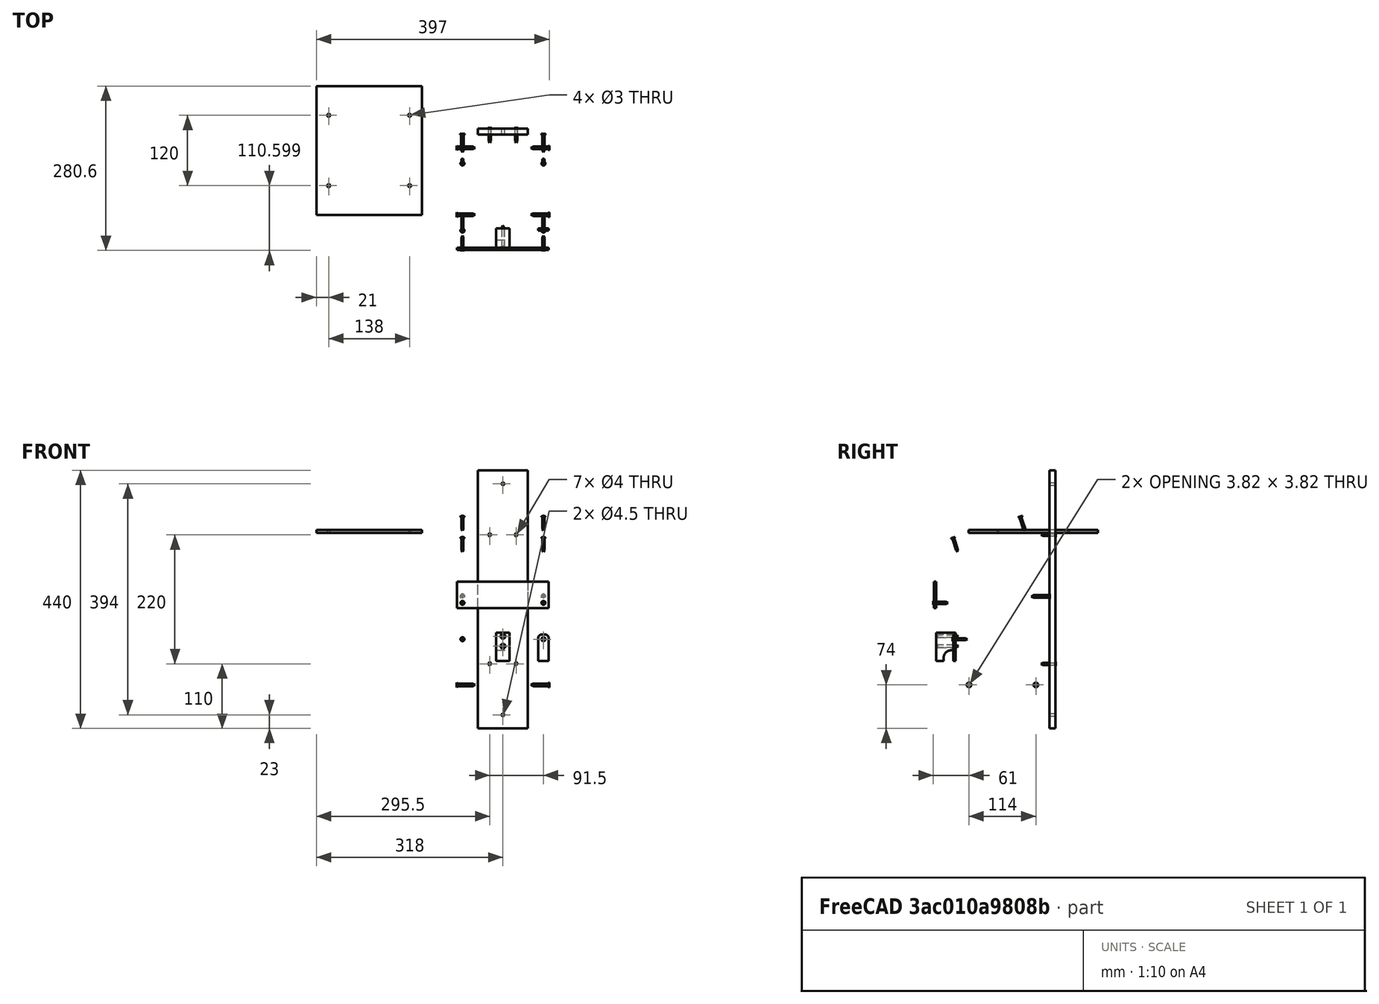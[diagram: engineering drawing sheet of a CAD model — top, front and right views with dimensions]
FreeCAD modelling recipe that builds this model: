
FCSTD DOCUMENT  (FreeCAD 1.0R39109 (Git))
Label: Nistkasten_LC_32__Final
License: All rights reserved
LicenseURL: http://en.wikipedia.org/wiki/All_rights_reserved
objects: TechDraw::DrawViewDimension×37, Sketcher::SketchObject×25, PartDesign::Body×25, Part::FeaturePython×20, TechDraw::DrawViewAnnotation×17, PartDesign::Pad×14, TechDraw::DrawProjGroupItem×13, PartDesign::FeatureBase×10, Part::Part2DObjectPython×10, PartDesign::Pocket×10, App::DocumentObjectGroup×6, PartDesign::Chamfer×6, TechDraw::DrawSVGTemplate×5, TechDraw::DrawProjGroup×5, TechDraw::DrawPage×5, Spreadsheet::Sheet×1, PartDesign::Fillet×1, TechDraw::DrawViewSection×1
note: 268 computed .brp shape members not serialized (recipe doc carries the construction recipe); baked Part::Feature solids carry a one-line shape summary decoded from their .brp

FEATURE [Sketcher::SketchObject] Sketch001
  ArcFitTolerance = 0
  AttachmentSupport = -> [XY_Plane001]
  FullyConstrained = true
  MakeInternals = false
  MapMode = 5
  expr: Constraints[42] = 120 mm / 2
  expr: Constraints[43] = 120 mm / 2
  expr: Constraints[8] = 120 mm + 2 * <<Parameter>>.Brettdicke
  expr: Constraints[9] = 124 mm + 2 * <<Parameter>>.Brettdicke
  sketch-geometry (16):
    g0: LineSegment [constr] StartX=-78 StartY=80 StartZ=0 EndX=78 EndY=80 EndZ=0
    g1: LineSegment [constr] StartX=78 StartY=80 StartZ=0 EndX=78 EndY=-80 EndZ=0
    g2: LineSegment [constr] StartX=78 StartY=-80 StartZ=0 EndX=-78 EndY=-80 EndZ=0
    g3: LineSegment [constr] StartX=-78 StartY=-80 StartZ=0 EndX=-78 EndY=80 EndZ=0
    g4: LineSegment StartX=-78 StartY=-25 StartZ=0 EndX=-78 EndY=25 EndZ=0
    g5: LineSegment StartX=-78 StartY=25 StartZ=0 EndX=-60 EndY=25 EndZ=0
    g6: LineSegment StartX=-60 StartY=25 StartZ=0 EndX=-60 EndY=80 EndZ=0
    g7: LineSegment StartX=-60 StartY=80 StartZ=0 EndX=60 EndY=80 EndZ=0
    g8: LineSegment StartX=60 StartY=80 StartZ=0 EndX=60 EndY=25 EndZ=0
    g9: LineSegment StartX=60 StartY=25 StartZ=0 EndX=78 EndY=25 EndZ=0
    g10: LineSegment StartX=78 StartY=25 StartZ=0 EndX=78 EndY=-25 EndZ=0
    g11: LineSegment StartX=78 StartY=-25 StartZ=0 EndX=60 EndY=-25 EndZ=0
    g12: LineSegment StartX=60 StartY=-25 StartZ=0 EndX=60 EndY=-80 EndZ=0
    g13: LineSegment StartX=60 StartY=-80 StartZ=0 EndX=-60 EndY=-80 EndZ=0
    g14: LineSegment StartX=-60 StartY=-80 StartZ=0 EndX=-60 EndY=-25 EndZ=0
    g15: LineSegment StartX=-60 StartY=-25 StartZ=0 EndX=-78 EndY=-25 EndZ=0
  constraints (46):
    c: Coincident(g0,g1)
    c: Coincident(g1,g2)
    c: Coincident(g2,g3)
    c: Coincident(g3,g0)
    c: Horizontal(g2)
    c: Vertical(g1)
    c: Symmetric(g0,g0,g-2)
    c: Symmetric(g2,g0,g-1)
    c: DistanceX(g2,g2) = 156
    c: DistanceY(g3,g3) = 160
    c: PointOnObject(g4,g3)
    c: PointOnObject(g4,g3)
    c: Coincident(g4,g5)
    c: Horizontal(g5)
    c: Coincident(g5,g6)
    c: PointOnObject(g6,g0)
    c: Vertical(g6)
    c: Coincident(g6,g7)
    c: PointOnObject(g7,g0)
    c: Coincident(g7,g8)
    c: Vertical(g8)
    c: Coincident(g8,g9)
    c: PointOnObject(g9,g1)
    c: Horizontal(g9)
    c: Coincident(g9,g10)
    c: PointOnObject(g10,g1)
    c: Coincident(g10,g11)
    c: Horizontal(g11)
    c: Coincident(g11,g12)
    c: PointOnObject(g12,g2)
    c: Vertical(g12)
    c: Coincident(g12,g13)
    c: PointOnObject(g13,g2)
    c: Coincident(g13,g14)
    c: Vertical(g14)
    c: Coincident(g14,g15)
    c: Coincident(g15,g4)
    c: Horizontal(g15)
    c: DistanceY(g4,g4) = 50
    c: Equal(g4,g10)
    c: DistanceY(g6,g6) = 55
    c: Equal(g8,g6)
    c: DistanceX(g14,g-1) = 60
    c: DistanceX(g-1,g11) = 60
    c: Equal(g15,g5)
    c: Equal(g5,g9)
FEATURE [Spreadsheet::Sheet] Spreadsheet  label="Parameter"
  cells = A2='Parameter; A3='Brettdicke; B3(Brettdicke)==18 mm
FEATURE [PartDesign::Pad] Pad001
  Direction = (0,0,1)
  Length = 18
  Length2 = 10
  Profile = -> Sketch001
  ReferenceAxis = -> Sketch001 [N_Axis]
  Reversed = true
  Suppressed = false
  Type = 0
  expr: Length = <<Parameter>>.Brettdicke
FEATURE [Sketcher::SketchObject] Sketch002
  ArcFitTolerance = 0
  AttachmentSupport = -> [XZ_Plane002]
  FullyConstrained = true
  MakeInternals = false
  MapMode = 5
  Placement = pos=(0,0,0) rot=(1,0,0;1.5708rad)
  expr: Constraints[39] = 156 mm - 2 * <<Parameter>>.Brettdicke
  expr: Constraints[9] = 120 mm + 2 * <<Parameter>>.Brettdicke
  sketch-geometry (16):
    g0: LineSegment [constr] StartX=-78 StartY=0 StartZ=0 EndX=78 EndY=0 EndZ=0
    g1: LineSegment [constr] StartX=78 StartY=0 StartZ=0 EndX=78 EndY=282 EndZ=0
    g2: LineSegment [constr] StartX=78 StartY=282 StartZ=0 EndX=-78 EndY=282 EndZ=0
    g3: LineSegment [constr] StartX=-78 StartY=282 StartZ=0 EndX=-78 EndY=0 EndZ=0
    g4: LineSegment StartX=-60 StartY=0 StartZ=0 EndX=-60 EndY=102 EndZ=0
    g5: LineSegment StartX=-60 StartY=102 StartZ=0 EndX=-78 EndY=102 EndZ=0
    g6: LineSegment StartX=-78 StartY=102 StartZ=0 EndX=-78 EndY=182 EndZ=0
    g7: LineSegment StartX=-78 StartY=182 StartZ=0 EndX=-60 EndY=182 EndZ=0
    g8: LineSegment StartX=-60 StartY=182 StartZ=0 EndX=-60 EndY=282 EndZ=0
    g9: LineSegment StartX=-60 StartY=282 StartZ=0 EndX=60 EndY=282 EndZ=0
    g10: LineSegment StartX=60 StartY=282 StartZ=0 EndX=60 EndY=182 EndZ=0
    g11: LineSegment StartX=60 StartY=182 StartZ=0 EndX=78 EndY=182 EndZ=0
    g12: LineSegment StartX=78 StartY=182 StartZ=0 EndX=78 EndY=102 EndZ=0
    g13: LineSegment StartX=78 StartY=102 StartZ=0 EndX=60 EndY=102 EndZ=0
    g14: LineSegment StartX=60 StartY=102 StartZ=0 EndX=60 EndY=0 EndZ=0
    g15: LineSegment StartX=60 StartY=0 StartZ=0 EndX=-60 EndY=0 EndZ=0
  constraints (45):
    c: Coincident(g0,g1)
    c: Coincident(g1,g2)
    c: Coincident(g2,g3)
    c: Coincident(g3,g0)
    c: Horizontal(g2)
    c: Vertical(g1)
    c: Vertical(g3)
    c: PointOnObject(g0,g-1)
    c: Symmetric(g0,g0,g-2)
    c: DistanceX(g0,g0) = 156
    c: DistanceY(g3,g3) = 282
    c: PointOnObject(g4,g0)
    c: Vertical(g4)
    c: Coincident(g4,g5)
    c: PointOnObject(g5,g3)
    c: Horizontal(g5)
    c: Coincident(g5,g6)
    c: PointOnObject(g6,g3)
    c: Coincident(g6,g7)
    c: Horizontal(g7)
    c: Coincident(g7,g8)
    c: PointOnObject(g8,g2)
    c: Vertical(g8)
    c: Coincident(g8,g9)
    c: Coincident(g9,g10)
    c: Vertical(g10)
    c: Coincident(g10,g11)
    c: PointOnObject(g11,g1)
    c: Horizontal(g11)
    c: Coincident(g11,g12)
    c: PointOnObject(g12,g1)
    c: Coincident(g12,g13)
    c: Horizontal(g13)
    c: Coincident(g13,g14)
    c: Vertical(g14)
    c: Coincident(g14,g15)
    c: Coincident(g15,g4)
    c: Symmetric(g4,g14,g-2)
    c: Symmetric(g8,g9,g-2)
    c: DistanceX(g15,g15) = 120
    c: DistanceY(g6,g6) = 80
    c: Equal(g6,g12)
    c: DistanceY(g4,g4) = 102
    c: Equal(g4,g14)
    c: Equal(g5,g7)
FEATURE [PartDesign::Pad] Pad002
  Direction = (0,-1,2e-16)
  Length = 18
  Length2 = 10
  Placement = pos=(0,0,0) rot=(1,0,0;1.5708rad)
  Profile = -> Sketch002
  ReferenceAxis = -> Sketch002 [N_Axis]
  Reversed = true
  Suppressed = false
  Type = 0
  expr: Length = <<Parameter>>.Brettdicke
FEATURE [Sketcher::SketchObject] Sketch003
  ArcFitTolerance = 0
  AttachmentSupport = -> [YZ_Plane003]
  FullyConstrained = true
  MakeInternals = false
  MapMode = 5
  Placement = pos=(0,0,0) rot=(0.57735,0.57735,0.57735;2.0944rad)
  expr: Constraints[33] = <<Parameter>>.Brettdicke
  expr: Constraints[35] = <<Parameter>>.Brettdicke
  expr: Constraints[36] = <<Parameter>>.Brettdicke
  expr: Constraints[42] = <<Parameter>>.Brettdicke
  expr: Constraints[45] = <<Parameter>>.Brettdicke
  expr: Constraints[59] = <<Parameter>>.Brettdicke
  expr: Constraints[60] = <<Parameter>>.Brettdicke
  sketch-geometry (25):
    g0: LineSegment StartX=-80 StartY=-18 StartZ=0 EndX=-80 EndY=0 EndZ=0
    g1: LineSegment StartX=-80 StartY=0 StartZ=0 EndX=-62 EndY=0 EndZ=0
    g2: LineSegment StartX=-95 StartY=193 StartZ=0 EndX=-113 EndY=193 EndZ=0
    g3: LineSegment StartX=-113 StartY=193 StartZ=0 EndX=-113 EndY=227.2 EndZ=0
    g4: LineSegment StartX=-113 StartY=227.2 StartZ=0 EndX=62 EndY=282 EndZ=0
    g5: LineSegment StartX=62 StartY=282 StartZ=0 EndX=80 EndY=282 EndZ=0
    g6: LineSegment StartX=80 StartY=282 StartZ=0 EndX=80 EndY=182 EndZ=0
    g7: LineSegment StartX=80 StartY=182 StartZ=0 EndX=62 EndY=182 EndZ=0
    g8: LineSegment StartX=62 StartY=182 StartZ=0 EndX=62 EndY=102 EndZ=0
    g9: LineSegment StartX=62 StartY=102 StartZ=0 EndX=80 EndY=102 EndZ=0
    g10: LineSegment StartX=80 StartY=102 StartZ=0 EndX=80 EndY=-18 EndZ=0
    g11: LineSegment StartX=80 StartY=-18 StartZ=0 EndX=25 EndY=-18 EndZ=0
    g12: LineSegment StartX=25 StartY=-18 StartZ=0 EndX=25 EndY=0 EndZ=0
    g13: LineSegment StartX=25 StartY=0 StartZ=0 EndX=-25 EndY=0 EndZ=0
    g14: LineSegment StartX=-25 StartY=0 StartZ=0 EndX=-25 EndY=-18 EndZ=0
    g15: LineSegment StartX=-25 StartY=-18 StartZ=0 EndX=-80 EndY=-18 EndZ=0
    g16: LineSegment StartX=-72 StartY=140 StartZ=0 EndX=-72 EndY=158 EndZ=0
    g17: LineSegment StartX=-72 StartY=158 StartZ=0 EndX=-95 EndY=158 EndZ=0
    g18: LineSegment StartX=-95 StartY=158 StartZ=0 EndX=-95 EndY=193 EndZ=0
    g19: LineSegment StartX=-80 StartY=80 StartZ=0 EndX=-113 EndY=122 EndZ=0
    g20: LineSegment StartX=-113 StartY=122 StartZ=0 EndX=-113 EndY=140 EndZ=0
    g21: LineSegment StartX=-113 StartY=140 StartZ=0 EndX=-72 EndY=140 EndZ=0
    g22: LineSegment StartX=-62 StartY=0 StartZ=0 EndX=-62 EndY=60 EndZ=0
    g23: LineSegment StartX=-62 StartY=60 StartZ=0 EndX=-80 EndY=60 EndZ=0
    g24: LineSegment StartX=-80 StartY=60 StartZ=0 EndX=-80 EndY=80 EndZ=0
  constraints (74):
    c: PointOnObject(g0,g-1)
    c: Vertical(g0)
    c: Coincident(g0,g1)
    c: PointOnObject(g1,g-1)
    c: Horizontal(g2)
    c: Coincident(g2,g3)
    c: Vertical(g3)
    c: Coincident(g3,g4)
    c: Coincident(g4,g5)
    c: Horizontal(g5)
    c: Coincident(g5,g6)
    c: Vertical(g6)
    c: Coincident(g6,g7)
    c: Horizontal(g7)
    c: Coincident(g7,g8)
    c: Vertical(g8)
    c: Coincident(g8,g9)
    c: Horizontal(g9)
    c: Coincident(g9,g10)
    c: Vertical(g10)
    c: Coincident(g10,g11)
    c: Horizontal(g11)
    c: Coincident(g11,g12)
    c: PointOnObject(g12,g-1)
    c: Vertical(g12)
    c: Coincident(g12,g13)
    c: Coincident(g13,g14)
    c: Vertical(g14)
    c: Coincident(g14,g15)
    c: Coincident(g15,g0)
    c: Horizontal(g15)
    c: Symmetric(g13,g12,g-2)
    c: DistanceX(g13,g13) = 50
    c: DistanceY(g14,g14) = 18
    c: DistanceX(g15,g15) = 55
    c: DistanceX(g1,g1) = 18
    c: DistanceX(g2,g2) = 18
    c: Equal(g12,g14)
    c: DistanceX(g11,g11) = 55
    c: DistanceY(g8,g8) = 80
    c: DistanceY(g10,g10) = 120
    c: DistanceY(g6,g6) = 100
    c: DistanceX(g5,g5) = 18
    c: DistanceY(g3,g3) = 34.2
    c: Equal(g9,g7)
    c: DistanceX(g7,g7) = 18
    c: Vertical(g16)
    c: Coincident(g16,g17)
    c: Horizontal(g17)
    c: Coincident(g17,g18)
    c: Coincident(g18,g2)
    c: Vertical(g18)
    c: DistanceX(g17,g17) = 23
    c: DistanceY(g18,g18) = 35
    c: Coincident(g19,g20)
    c: Vertical(g20)
    c: Coincident(g20,g21)
    c: Coincident(g21,g16)
    c: Horizontal(g21)
    c: DistanceY(g20,g20) = 18
    c: DistanceY(g16,g16) = 18
    c: DistanceY(g19,g20) = 60
    c: DistanceX(g19,g19) = 33
    c: DistanceX(g21,g21) = 41
    c: Coincident(g1,g22)
    c: Vertical(g22)
    c: Coincident(g22,g23)
    c: Horizontal(g23)
    c: Coincident(g23,g24)
    c: Coincident(g24,g19)
    c: Vertical(g24)
    c: DistanceY(g0,g19) = 80
    c: DistanceY(g24,g24) = 20
    c: DistanceX(g23,g23) = 18
FEATURE [PartDesign::Pad] Pad003
  Direction = (1,0,0)
  Length = 18
  Length2 = 10
  Placement = pos=(0,0,0) rot=(0.57735,0.57735,0.57735;2.0944rad)
  Profile = -> Sketch003
  ReferenceAxis = -> Sketch003 [N_Axis]
  Reversed = true
  Suppressed = false
  Type = 0
  expr: Length = <<Parameter>>.Brettdicke
FEATURE [Sketcher::SketchObject] Sketch004
  ArcFitTolerance = 0
  AttachmentSupport = -> [XY_Plane005]
  FullyConstrained = true
  MakeInternals = false
  MapMode = 5
  expr: Constraints[20] = <<Parameter>>.Brettdicke
  sketch-geometry (8):
    g0: LineSegment StartX=-60 StartY=0 StartZ=0 EndX=60 EndY=0 EndZ=0
    g1: LineSegment StartX=78 StartY=-53 StartZ=0 EndX=-78 EndY=-53 EndZ=0
    g2: LineSegment StartX=-78 StartY=-53 StartZ=0 EndX=-78 EndY=-12 EndZ=0
    g3: LineSegment StartX=-78 StartY=-12 StartZ=0 EndX=-60 EndY=-12 EndZ=0
    g4: LineSegment StartX=-60 StartY=-12 StartZ=0 EndX=-60 EndY=0 EndZ=0
    g5: LineSegment StartX=78 StartY=-53 StartZ=0 EndX=78 EndY=-12 EndZ=0
    g6: LineSegment StartX=78 StartY=-12 StartZ=0 EndX=60 EndY=-12 EndZ=0
    g7: LineSegment StartX=60 StartY=-12 StartZ=0 EndX=60 EndY=0 EndZ=0
  constraints (22):
    c: Horizontal(g1)
    c: PointOnObject(g0,g-1)
    c: Symmetric(g0,g0,g-2)
    c: DistanceY(g1,g0) = 53
    c: DistanceX(g1,g1) = 156
    c: Coincident(g1,g2)
    c: Vertical(g2)
    c: Coincident(g2,g3)
    c: Horizontal(g3)
    c: Coincident(g3,g4)
    c: Coincident(g4,g0)
    c: Vertical(g4)
    c: Coincident(g1,g5)
    c: Vertical(g5)
    c: Coincident(g5,g6)
    c: Horizontal(g6)
    c: Coincident(g6,g7)
    c: Coincident(g7,g0)
    c: Vertical(g7)
    c: Symmetric(g5,g2,g-2)
    c: DistanceX(g3,g3) = 18
    c: DistanceY(g4,g4) = 12
FEATURE [PartDesign::Pad] Pad004
  Direction = (0,0,1)
  Length = 18
  Length2 = 10
  Profile = -> Sketch004
  ReferenceAxis = -> Sketch004 [N_Axis]
  Suppressed = false
  Type = 0
  expr: Length = <<Parameter>>.Brettdicke
FEATURE [PartDesign::Body] Body005  label="Prädatorenschutz_Boden"
  AllowCompound = false
  Group = -> [Sketch004,Pad004]
  Origin = -> Origin005
  Placement = pos=(0,-60,140) rot=(0,0,1;0rad)
  Tip = -> Pad004
FEATURE [Sketcher::SketchObject] Sketch006
  ArcFitTolerance = 0
  AttachmentSupport = -> [XZ_Plane006]
  FullyConstrained = true
  MakeInternals = false
  MapMode = 5
  Placement = pos=(0,0,0) rot=(1,0,0;1.5708rad)
  expr: Constraints[25] = <<Parameter>>.Brettdicke
  sketch-geometry (13):
    g0: LineSegment [constr] StartX=-78 StartY=0 StartZ=0 EndX=78 EndY=0 EndZ=0
    g1: LineSegment [constr] StartX=78 StartY=0 StartZ=0 EndX=78 EndY=69 EndZ=0
    g2: LineSegment [constr] StartX=78 StartY=69 StartZ=0 EndX=-78 EndY=69 EndZ=0
    g3: LineSegment [constr] StartX=-78 StartY=69 StartZ=0 EndX=-78 EndY=0 EndZ=0
    g4: LineSegment StartX=-78 StartY=0 StartZ=0 EndX=-78 EndY=35 EndZ=0
    g5: LineSegment StartX=-78 StartY=35 StartZ=0 EndX=-60 EndY=35 EndZ=0
    g6: LineSegment StartX=-60 StartY=35 StartZ=0 EndX=-60 EndY=69 EndZ=0
    g7: LineSegment StartX=-60 StartY=69 StartZ=0 EndX=78 EndY=69 EndZ=0
    g8: LineSegment StartX=78 StartY=69 StartZ=0 EndX=78 EndY=0 EndZ=0
    g9: LineSegment StartX=78 StartY=0 StartZ=0 EndX=-78 EndY=0 EndZ=0
    g10: Circle CenterX=0 CenterY=34.5 CenterZ=0 NormalX=0 NormalY=0 NormalZ=1 AngleXU=0 Radius=22.5
    g11: LineSegment [constr] StartX=0 StartY=34.5 StartZ=0 EndX=0 EndY=0 EndZ=0
    g12: LineSegment [constr] StartX=0 StartY=34.5 StartZ=0 EndX=0 EndY=69 EndZ=0
  constraints (34):
    c: Coincident(g0,g1)
    c: Coincident(g1,g2)
    c: Coincident(g2,g3)
    c: Coincident(g3,g0)
    c: Horizontal(g2)
    c: Vertical(g1)
    c: Vertical(g3)
    c: PointOnObject(g0,g-1)
    c: Symmetric(g0,g0,g-2)
    c: DistanceX(g0,g0) = 156
    c: DistanceY(g3,g3) = 69
    c: Coincident(g0,g4)
    c: PointOnObject(g4,g3)
    c: Coincident(g4,g5)
    c: Horizontal(g5)
    c: Coincident(g5,g6)
    c: PointOnObject(g6,g2)
    c: Vertical(g6)
    c: Coincident(g6,g7)
    c: Coincident(g7,g1)
    c: Coincident(g7,g8)
    c: Coincident(g8,g0)
    c: Coincident(g8,g9)
    c: Coincident(g9,g4)
    c: DistanceY(g4,g4) = 35
    c: DistanceX(g5,g5) = 18
    c: PointOnObject(g10,g-2)
    c: Coincident(g11,g10)
    c: Coincident(g11,g-1)
    c: Coincident(g12,g10)
    c: PointOnObject(g12,g7)
    c: Vertical(g12)
    c: Equal(g12,g11)
    c: Diameter(g10) = 45
FEATURE [PartDesign::Pad] Pad005
  Direction = (0,-1,2e-16)
  Length = 18
  Length2 = 10
  Placement = pos=(0,0,0) rot=(1,0,0;1.5708rad)
  Profile = -> Sketch006
  ReferenceAxis = -> Sketch006 [N_Axis]
  Suppressed = false
  Type = 0
  expr: Length = <<Parameter>>.Brettdicke
FEATURE [PartDesign::Body] Body006  label="Einfluglochscheibe"
  AllowCompound = false
  Group = -> [Sketch006,Pad005]
  Origin = -> Origin006
  Placement = pos=(0,-95,158) rot=(0,0,1;0rad)
  Tip = -> Pad005
FEATURE [Sketcher::SketchObject] Sketch008
  ArcFitTolerance = 0
  AttachmentSupport = -> [XZ_Plane008]
  FullyConstrained = true
  MakeInternals = false
  MapMode = 5
  Placement = pos=(0,0,0) rot=(1,0,0;1.5708rad)
  expr: Constraints[22] = <<Parameter>>.Brettdicke + 0.5 mm
  sketch-geometry (8):
    g0: LineSegment StartX=-78 StartY=0 StartZ=0 EndX=-78 EndY=60 EndZ=0
    g1: LineSegment StartX=-78 StartY=60 StartZ=0 EndX=-59.5 EndY=60 EndZ=0
    g2: LineSegment StartX=-59.5 StartY=60 StartZ=0 EndX=-59.5 EndY=140 EndZ=0
    g3: LineSegment StartX=-59.5 StartY=140 StartZ=0 EndX=59.5 EndY=140 EndZ=0
    g4: LineSegment StartX=59.5 StartY=140 StartZ=0 EndX=59.5 EndY=60 EndZ=0
    g5: LineSegment StartX=59.5 StartY=60 StartZ=0 EndX=78 EndY=60 EndZ=0
    g6: LineSegment StartX=78 StartY=60 StartZ=0 EndX=78 EndY=0 EndZ=0
    g7: LineSegment StartX=78 StartY=0 StartZ=0 EndX=-78 EndY=0 EndZ=0
  constraints (23):
    c: PointOnObject(g0,g-1)
    c: Vertical(g0)
    c: Coincident(g0,g1)
    c: Horizontal(g1)
    c: Coincident(g1,g2)
    c: Vertical(g2)
    c: Coincident(g2,g3)
    c: Horizontal(g3)
    c: Coincident(g3,g4)
    c: Vertical(g4)
    c: Coincident(g4,g5)
    c: Horizontal(g5)
    c: Coincident(g5,g6)
    c: Vertical(g6)
    c: Coincident(g6,g7)
    c: Coincident(g7,g0)
    c: Symmetric(g0,g6,g-2)
    c: DistanceX(g7,g7) = 156
    c: DistanceY(g0,g0) = 60
    c: Equal(g0,g6)
    c: DistanceY(g2,g2) = 80
    c: Equal(g1,g5)
    c: DistanceX(g1,g1) = 18.5
FEATURE [PartDesign::Pad] Pad006
  Direction = (0,-1,2e-16)
  Length = 18
  Length2 = 10
  Placement = pos=(0,0,0) rot=(1,0,0;1.5708rad)
  Profile = -> Sketch008
  ReferenceAxis = -> Sketch008 [N_Axis]
  Suppressed = false
  Type = 0
  expr: Length = <<Parameter>>.Brettdicke
FEATURE [Sketcher::SketchObject] Sketch009
  ArcFitTolerance = 0
  AttachmentSupport = -> [XY_Plane009]
  FullyConstrained = true
  MakeInternals = false
  MapMode = 5
  expr: Constraints[8] = 160 + 20
  expr: Constraints[9] = 180 + 40
  sketch-geometry (4):
    g0: LineSegment StartX=-90 StartY=110 StartZ=0 EndX=90 EndY=110 EndZ=0
    g1: LineSegment StartX=90 StartY=110 StartZ=0 EndX=90 EndY=-110 EndZ=0
    g2: LineSegment StartX=90 StartY=-110 StartZ=0 EndX=-90 EndY=-110 EndZ=0
    g3: LineSegment StartX=-90 StartY=-110 StartZ=0 EndX=-90 EndY=110 EndZ=0
  constraints (10):
    c: Coincident(g0,g1)
    c: Coincident(g1,g2)
    c: Coincident(g2,g3)
    c: Coincident(g3,g0)
    c: Horizontal(g2)
    c: Vertical(g1)
    c: Symmetric(g0,g0,g-2)
    c: Symmetric(g2,g0,g-1)
    c: DistanceX(g2,g2) = 180
    c: DistanceY(g3,g3) = 220
FEATURE [PartDesign::Pad] Pad007
  Direction = (0,0,1)
  Length = 5
  Length2 = 10
  Profile = -> Sketch009
  ReferenceAxis = -> Sketch009 [N_Axis]
  Suppressed = false
  Type = 0
FEATURE [Sketcher::SketchObject] Sketch010
  ArcFitTolerance = 0
  AttachmentSupport = -> [XY_Plane010]
  FullyConstrained = true
  MakeInternals = false
  MapMode = 5
  sketch-geometry (4):
    g0: LineSegment StartX=150 StartY=100 StartZ=0 EndX=1450 EndY=100 EndZ=0
    g1: LineSegment StartX=1450 StartY=100 StartZ=0 EndX=1450 EndY=-100 EndZ=0
    g2: LineSegment StartX=1450 StartY=-100 StartZ=0 EndX=150 EndY=-100 EndZ=0
    g3: LineSegment StartX=150 StartY=-100 StartZ=0 EndX=150 EndY=100 EndZ=0
  constraints (11):
    c: Coincident(g0,g1)
    c: Coincident(g1,g2)
    c: Coincident(g2,g3)
    c: Coincident(g3,g0)
    c: Horizontal(g0)
    c: Horizontal(g2)
    c: Vertical(g1)
    c: Symmetric(g2,g0,g-1)
    c: DistanceX(g-1,g0) = 150
    c: DistanceY(g3,g3) = 200
    c: DistanceX(g2,g2) = 1300
FEATURE [PartDesign::Body] Body010  label="Brett_Umriss"
  AllowCompound = false
  Group = -> [Sketch010]
  Origin = -> Origin010
FEATURE [PartDesign::FeatureBase] Clone005
  BaseFeature = -> Body005
  Placement = pos=(0,-60,140) rot=(0,0,1;0rad)
  Suppressed = false
FEATURE [PartDesign::Body] Body014  label="LC_Prädatorenschutz_Boden"
  AllowCompound = false
  BaseFeature = -> Body005
  Group = -> [Clone005]
  Origin = -> Origin014
  Placement = pos=(1430,10,-72) rot=(0,0,-1;1.5708rad)
  Tip = -> Clone005
FEATURE [PartDesign::FeatureBase] Clone006
  BaseFeature = -> Body006
  Placement = pos=(0,-95,160) rot=(0,0,1;0rad)
  Suppressed = false
FEATURE [PartDesign::Body] Body015  label="LC_Einflugloch"
  AllowCompound = false
  BaseFeature = -> Body006
  Group = -> [Clone006]
  Origin = -> Origin015
  Placement = pos=(1214,10,-26) rot=(0.57735,-0.57735,0.57735;4.18879rad)
  Tip = -> Clone006
FEATURE [Part::Part2DObjectPython] Shape2DView004  label="LCs_Prädatorenschutz_Boden"  # Draft 2D object (typed FeaturePython)
  AutoUpdate = true
  Base = -> Body014
  Clip = false
  FuseArch = false
  HiddenLines = false
  InPlace = true
  OnlySolids = false
  Projection = (0,0,1)
  ProjectionMode = 0
  SegmentLength = 0.05
  Tessellation = false
  VisibleOnly = false
FEATURE [Part::Part2DObjectPython] Shape2DView005  label="LCs_Einflugloch"  # Draft 2D object (typed FeaturePython)
  AutoUpdate = true
  Base = -> Body015
  Clip = false
  FuseArch = false
  HiddenLines = false
  InPlace = true
  OnlySolids = false
  Projection = (0,0,1)
  ProjectionMode = 0
  SegmentLength = 0.05
  Tessellation = false
  VisibleOnly = false
FEATURE [Sketcher::SketchObject] Sketch011
  ArcFitTolerance = 0
  AttachmentSupport = -> [XZ_Plane018]
  FullyConstrained = true
  MakeInternals = false
  MapMode = 5
  Placement = pos=(0,0,0) rot=(1,0,0;1.5708rad)
  sketch-geometry (4):
    g0: LineSegment StartX=-78 StartY=0 StartZ=0 EndX=78 EndY=2e-16 EndZ=0
    g1: LineSegment StartX=78 StartY=2e-16 StartZ=0 EndX=78 EndY=45 EndZ=0
    g2: LineSegment StartX=78 StartY=45 StartZ=0 EndX=-78 EndY=45 EndZ=0
    g3: LineSegment StartX=-78 StartY=45 StartZ=0 EndX=-78 EndY=0 EndZ=0
  constraints (11):
    c: Coincident(g0,g1)
    c: Coincident(g1,g2)
    c: Coincident(g2,g3)
    c: Coincident(g3,g0)
    c: Horizontal(g2)
    c: Vertical(g1)
    c: Vertical(g3)
    c: PointOnObject(g0,g-1)
    c: Symmetric(g0,g0,g-2)
    c: DistanceX(g0,g0) = 156
    c: DistanceY(g3,g3) = 45
FEATURE [PartDesign::Pad] Pad008
  Direction = (0,-1,2e-16)
  Length = 4
  Length2 = 10
  Placement = pos=(0,0,0) rot=(1,0,0;1.5708rad)
  Profile = -> Sketch011
  ReferenceAxis = -> Sketch011 [N_Axis]
  Suppressed = false
  Type = 0
FEATURE [Sketcher::SketchObject] Sketch012
  ArcFitTolerance = 0
  AttachmentSupport = -> [Pad001]
  FullyConstrained = true
  MakeInternals = false
  MapMode = 5
  Placement = pos=(0,0,-18) rot=(1,0,0;3.14159rad)
  sketch-geometry (8):
    g0: LineSegment [constr] StartX=-40 StartY=50 StartZ=0 EndX=40 EndY=50 EndZ=0
    g1: LineSegment [constr] StartX=40 StartY=50 StartZ=0 EndX=40 EndY=-50 EndZ=0
    g2: LineSegment [constr] StartX=40 StartY=-50 StartZ=0 EndX=-40 EndY=-50 EndZ=0
    g3: LineSegment [constr] StartX=-40 StartY=-50 StartZ=0 EndX=-40 EndY=50 EndZ=0
    g4: Circle CenterX=-40 CenterY=50 CenterZ=0 NormalX=0 NormalY=0 NormalZ=1 AngleXU=0 Radius=3
    g5: Circle CenterX=40 CenterY=50 CenterZ=0 NormalX=0 NormalY=0 NormalZ=1 AngleXU=0 Radius=3
    g6: Circle CenterX=40 CenterY=-50 CenterZ=0 NormalX=0 NormalY=0 NormalZ=1 AngleXU=0 Radius=3
    g7: Circle CenterX=-40 CenterY=-50 CenterZ=0 NormalX=0 NormalY=0 NormalZ=1 AngleXU=0 Radius=3
  constraints (18):
    c: Coincident(g0,g1)
    c: Coincident(g1,g2)
    c: Coincident(g2,g3)
    c: Coincident(g3,g0)
    c: Horizontal(g0)
    c: Vertical(g1)
    c: Symmetric(g2,g1,g-2)
    c: Symmetric(g2,g0,g-1)
    c: DistanceX(g2,g2) = 80
    c: Coincident(g4,g0)
    c: Coincident(g5,g0)
    c: Coincident(g6,g1)
    c: Coincident(g7,g2)
    c: Equal(g4,g5)
    c: Equal(g5,g6)
    c: Equal(g6,g7)
    c: Diameter(g4) = 6
    c: DistanceY(g3,g3) = 100
FEATURE [PartDesign::Pocket] Pocket001
  BaseFeature = -> Pad001
  Direction = (0,0,1)
  Length = 5
  Length2 = 5
  Profile = -> Sketch012
  ReferenceAxis = -> Sketch012 [N_Axis]
  Suppressed = false
  Type = 1
FEATURE [PartDesign::Body] Body001  label="Boden"
  AllowCompound = false
  Group = -> [Sketch001,Pad001,Sketch012,Pocket001]
  Origin = -> Origin001
  Tip = -> Pocket001
FEATURE [PartDesign::FeatureBase] Clone008
  BaseFeature = -> Body001
  Suppressed = false
FEATURE [PartDesign::Body] Body017  label="LC_Boden"
  AllowCompound = false
  BaseFeature = -> Body001
  Group = -> [Clone008]
  Origin = -> Origin017
  Placement = pos=(1233,10,89) rot=(0,0,-1;1.5708rad)
  Tip = -> Clone008
FEATURE [Part::Part2DObjectPython] Shape2DView007  label="LCs_Boden"  # Draft 2D object (typed FeaturePython)
  AutoUpdate = true
  Base = -> Body017
  Clip = false
  FuseArch = false
  HiddenLines = false
  InPlace = true
  OnlySolids = false
  Projection = (0,0,1)
  ProjectionMode = 0
  SegmentLength = 0.05
  Tessellation = false
  VisibleOnly = false
FEATURE [Sketcher::SketchObject] Sketch013
  ArcFitTolerance = 0
  AttachmentSupport = -> [Pad006]
  FullyConstrained = true
  MakeInternals = false
  MapMode = 5
  Placement = pos=(0,-18,0) rot=(1,0,0;1.5708rad)
  sketch-geometry (3):
    g0: LineSegment [constr] StartX=-40 StartY=12 StartZ=0 EndX=40 EndY=12 EndZ=0
    g1: Circle CenterX=-40 CenterY=12 CenterZ=0 NormalX=0 NormalY=0 NormalZ=1 AngleXU=0 Radius=1.5
    g2: Circle CenterX=40 CenterY=12 CenterZ=0 NormalX=0 NormalY=0 NormalZ=1 AngleXU=0 Radius=1.5
  constraints (7):
    c: Symmetric(g0,g0,g-2)
    c: DistanceX(g0,g0) = 80
    c: Coincident(g1,g0)
    c: Coincident(g2,g0)
    c: Equal(g1,g2)
    c: Diameter(g1) = 3
    c: DistanceY(g-1,g1) = 12
FEATURE [PartDesign::Pocket] Pocket002
  BaseFeature = -> Pad006
  Direction = (0,1,-2e-16)
  Length = 5
  Length2 = 5
  Placement = pos=(0,0,0) rot=(1,0,0;1.5708rad)
  Profile = -> Sketch013
  ReferenceAxis = -> Sketch013 [N_Axis]
  Suppressed = false
  Type = 1
FEATURE [PartDesign::Body] Body008  label="Tür_Frontplatte"
  AllowCompound = false
  Group = -> [Sketch008,Pad006,Sketch013,Pocket002]
  Origin = -> Origin008
  Placement = pos=(0,-62,0) rot=(0,0,1;0rad)
  Tip = -> Pocket002
FEATURE [PartDesign::FeatureBase] Clone007
  BaseFeature = -> Body008
  Placement = pos=(0,-60,0) rot=(0,0,1;0rad)
  Suppressed = false
FEATURE [PartDesign::Body] Body016  label="LC_Front_Abdeckung"
  AllowCompound = false
  BaseFeature = -> Body008
  Group = -> [Clone007]
  Origin = -> Origin016
  Placement = pos=(1009,9,8) rot=(0.57735,-0.57735,0.57735;4.18879rad)
  Tip = -> Clone007
FEATURE [Part::Part2DObjectPython] Shape2DView006  label="LCs_Front_Abdeckung"  # Draft 2D object (typed FeaturePython)
  AutoUpdate = true
  Base = -> Body016
  Clip = false
  FuseArch = false
  HiddenLines = false
  InPlace = true
  OnlySolids = false
  Projection = (0,0,1)
  ProjectionMode = 0
  SegmentLength = 0.05
  Tessellation = false
  VisibleOnly = false
FEATURE [Sketcher::SketchObject] Sketch015
  ArcFitTolerance = 0
  AttachmentSupport = -> [Pad003]
  FullyConstrained = true
  MakeInternals = false
  MapMode = 5
  Placement = pos=(-18,0,0) rot=(0.57735,0.57735,-0.57735;4.18879rad)
  sketch-geometry (2):
    g0: Circle CenterX=-57 CenterY=9 CenterZ=0 NormalX=0 NormalY=0 NormalZ=1 AngleXU=0 Radius=1.5
    g1: Circle CenterX=57 CenterY=9 CenterZ=0 NormalX=0 NormalY=0 NormalZ=1 AngleXU=0 Radius=1.5
  constraints (5):
    c: Diameter(g0) = 3
    c: DistanceY(g-1,g0) = 9
    c: DistanceX(g0,g-1) = 57
    c: Equal(g1,g0)
    c: Symmetric(g1,g0,g-2)
FEATURE [PartDesign::Pocket] Pocket
  BaseFeature = -> Pad003
  Direction = (1,0,0)
  Length = 5
  Length2 = 5
  Placement = pos=(0,0,0) rot=(0.57735,0.57735,0.57735;2.0944rad)
  Profile = -> Sketch015
  ReferenceAxis = -> Sketch015 [N_Axis]
  Suppressed = false
  Type = 1
FEATURE [Sketcher::SketchObject] Sketch017
  ArcFitTolerance = 0
  AttachmentSupport = -> [Pad002]
  FullyConstrained = true
  MakeInternals = false
  MapMode = 5
  Placement = pos=(0,18,0) rot=(-1,0,0;1.5708rad)
  sketch-geometry (2):
    g0: Circle CenterX=69 CenterY=-142 CenterZ=0 NormalX=0 NormalY=0 NormalZ=1 AngleXU=0 Radius=1.5
    g1: Circle CenterX=-69 CenterY=-142 CenterZ=0 NormalX=0 NormalY=0 NormalZ=1 AngleXU=0 Radius=1.5
  constraints (5):
    c: Equal(g0,g1)
    c: Symmetric(g0,g1,g-2)
    c: DistanceX(g-1,g0) = 69
    c: DistanceY(g0,g-1) = 142
    c: Diameter(g0) = 3
FEATURE [PartDesign::Pocket] Pocket004
  BaseFeature = -> Pad002
  Direction = (0,-1,-2e-16)
  Length = 5
  Length2 = 5
  Placement = pos=(0,0,0) rot=(1,0,0;1.5708rad)
  Profile = -> Sketch017
  ReferenceAxis = -> Sketch017 [N_Axis]
  Suppressed = false
  Type = 1
FEATURE [PartDesign::Body] Body002  label="Hinten"
  AllowCompound = false
  Group = -> [Sketch002,Pad002,Sketch017,Pocket004]
  Origin = -> Origin002
  Placement = pos=(0,62,0) rot=(0,0,1;0rad)
  Tip = -> Pocket004
FEATURE [PartDesign::FeatureBase] Clone004
  BaseFeature = -> Body002
  Placement = pos=(0,60,0) rot=(0,0,1;0rad)
  Suppressed = false
FEATURE [PartDesign::Body] Body013  label="LC_Hinten"
  AllowCompound = false
  BaseFeature = -> Body002
  Group = -> [Clone004]
  Origin = -> Origin013
  Placement = pos=(1005,10,148) rot=(0.57735,0.57735,-0.57735;4.18879rad)
  Tip = -> Clone004
FEATURE [Part::Part2DObjectPython] Shape2DView003  label="LCs_Hinten"  # Draft 2D object (typed FeaturePython)
  AutoUpdate = true
  Base = -> Body013
  Clip = false
  FuseArch = false
  HiddenLines = false
  InPlace = true
  OnlySolids = false
  Projection = (0,0,1)
  ProjectionMode = 0
  SegmentLength = 0.05
  Tessellation = false
  VisibleOnly = false
FEATURE [Sketcher::SketchObject] Sketch018
  ArcFitTolerance = 0
  AttachmentSupport = -> [Pocket]
  ExternalGeometry = -> [Pocket]
  FullyConstrained = true
  MakeInternals = false
  MapMode = 5
  Placement = pos=(0,3.08e-14,140) rot=(0,0,-1;1.5708rad)
  sketch-geometry (4):
    g0: LineSegment StartX=72 StartY=-18 StartZ=0 EndX=113 EndY=-18 EndZ=0
    g1: LineSegment StartX=113 StartY=-18 StartZ=0 EndX=113 EndY=0 EndZ=0
    g2: LineSegment StartX=113 StartY=0 StartZ=0 EndX=72 EndY=0 EndZ=0
    g3: LineSegment StartX=72 StartY=0 StartZ=0 EndX=72 EndY=-18 EndZ=0
  constraints (10):
    c: Coincident(g0,g1)
    c: Coincident(g1,g2)
    c: Coincident(g2,g3)
    c: Coincident(g3,g0)
    c: Horizontal(g2)
    c: Vertical(g1)
    c: Vertical(g3)
    c: Coincident(g0,g-3)
    c: PointOnObject(g1,g-1)
    c: Coincident(g0,g-3)
FEATURE [PartDesign::Pocket] Pocket005
  BaseFeature = -> Pocket
  Direction = (0,0,-1)
  Length = 0.5
  Length2 = 5
  Placement = pos=(0,0,0) rot=(0.57735,0.57735,0.57735;2.0944rad)
  Profile = -> Sketch018
  ReferenceAxis = -> Sketch018 [N_Axis]
  Suppressed = false
  Type = 0
FEATURE [PartDesign::Body] Body003  label="Links"
  AllowCompound = false
  Group = -> [Sketch003,Pad003,Sketch015,Pocket,Sketch018,Pocket005]
  Origin = -> Origin003
  Placement = pos=(-60,0,0) rot=(0,0,1;0rad)
  Tip = -> Pocket005
FEATURE [PartDesign::FeatureBase] Clone
  BaseFeature = -> Body003
  Placement = pos=(-70,0,0) rot=(0,0,1;0rad)
  Suppressed = false
FEATURE [PartDesign::FeatureBase] Clone002
  BaseFeature = -> Body003
  Placement = pos=(-70,0,0) rot=(0,0,1;0rad)
  Suppressed = false
FEATURE [PartDesign::Body] Body011  label="LC_Links"
  AllowCompound = false
  BaseFeature = -> Body003
  Group = -> [Clone002]
  Origin = -> Origin011
  Placement = pos=(179,17,3.6e-14) rot=(0,1,0;1.5708rad)
  Tip = -> Clone002
FEATURE [Part::Part2DObjectPython] Shape2DView001  label="LCs_Links"  # Draft 2D object (typed FeaturePython)
  AutoUpdate = true
  Base = -> Body011
  Clip = false
  FuseArch = false
  HiddenLines = false
  InPlace = true
  OnlySolids = false
  Projection = (0,0,1)
  ProjectionMode = 0
  SegmentLength = 0.05
  Tessellation = false
  VisibleOnly = false
FEATURE [Sketcher::SketchObject] Sketch019
  ArcFitTolerance = 0
  AttachmentSupport = -> [Clone]
  ExternalGeometry = -> [Clone]
  FullyConstrained = true
  MakeInternals = false
  MapMode = 5
  Placement = pos=(-70,-113,6.33e-14) rot=(1,0,0;1.5708rad)
  sketch-geometry (4):
    g0: LineSegment StartX=-18 StartY=193 StartZ=0 EndX=0 EndY=193 EndZ=0
    g1: LineSegment StartX=0 StartY=193 StartZ=0 EndX=0 EndY=243 EndZ=0
    g2: LineSegment StartX=0 StartY=243 StartZ=0 EndX=-18 EndY=243 EndZ=0
    g3: LineSegment StartX=-18 StartY=243 StartZ=0 EndX=-18 EndY=193 EndZ=0
  constraints (11):
    c: Coincident(g0,g1)
    c: Coincident(g1,g2)
    c: Coincident(g2,g3)
    c: Coincident(g3,g0)
    c: Horizontal(g0)
    c: Horizontal(g2)
    c: Vertical(g1)
    c: Vertical(g3)
    c: Coincident(g0,g-3)
    c: PointOnObject(g1,g-2)
    c: DistanceY(g1,g1) = 50
FEATURE [PartDesign::Pocket] Pocket006
  BaseFeature = -> Clone
  Direction = (0,1,-1.1e-15)
  Length = 18
  Length2 = 5
  Placement = pos=(-70,0,0) rot=(0,0,1;0rad)
  Profile = -> Sketch019
  ReferenceAxis = -> Sketch019 [N_Axis]
  Suppressed = false
  Type = 0
FEATURE [PartDesign::Body] Body004  label="Rechts (clone)"
  AllowCompound = false
  BaseFeature = -> Body003
  Group = -> [Clone,Sketch019,Pocket006]
  Origin = -> Origin004
  Placement = pos=(148,0,0) rot=(0,0,1;0rad)
  Tip = -> Pocket006
FEATURE [PartDesign::FeatureBase] Clone003
  BaseFeature = -> Body004
  Placement = pos=(160,0,0) rot=(0,0,1;0rad)
  Suppressed = false
FEATURE [PartDesign::Body] Body012  label="LC_Rechts"
  AllowCompound = false
  BaseFeature = -> Body004
  Group = -> [Clone003]
  Origin = -> Origin012
  Placement = pos=(699,-17,158) rot=(0.707107,0,-0.707107;3.14159rad)
  Tip = -> Clone003
FEATURE [App::DocumentObjectGroup] Group002  label="Lasercutting_Bauteile"
  Group = -> [Body010,Body011,Body012,Body013,Body014,Body015,Body016,Body017]
FEATURE [Part::Part2DObjectPython] Shape2DView002  label="LCs_Rechts"  # Draft 2D object (typed FeaturePython)
  AutoUpdate = true
  Base = -> Body012
  Clip = false
  FuseArch = false
  HiddenLines = false
  InPlace = true
  OnlySolids = false
  Projection = (0,0,1)
  ProjectionMode = 0
  SegmentLength = 0.05
  Tessellation = false
  VisibleOnly = false
FEATURE [App::DocumentObjectGroup] Group003  label="Lasercutting_Schnittlinien"
  Group = -> [Shape2DView001,Shape2DView002,Shape2DView003,Shape2DView004,Shape2DView005,Shape2DView006,Shape2DView007]
FEATURE [Sketcher::SketchObject] Sketch020
  ArcFitTolerance = 0
  AttachmentSupport = -> [XZ_Plane019]
  FullyConstrained = true
  MakeInternals = false
  MapMode = 5
  Placement = pos=(0,0,0) rot=(1,0,0;1.5708rad)
  expr: Constraints[25] = <<Parameter>>.Brettdicke
  sketch-geometry (13):
    g0: LineSegment [constr] StartX=-78 StartY=0 StartZ=0 EndX=78 EndY=0 EndZ=0
    g1: LineSegment [constr] StartX=78 StartY=0 StartZ=0 EndX=78 EndY=69 EndZ=0
    g2: LineSegment [constr] StartX=78 StartY=69 StartZ=0 EndX=-78 EndY=69 EndZ=0
    g3: LineSegment [constr] StartX=-78 StartY=69 StartZ=0 EndX=-78 EndY=0 EndZ=0
    g4: LineSegment StartX=-78 StartY=0 StartZ=0 EndX=-78 EndY=35 EndZ=0
    g5: LineSegment StartX=-78 StartY=35 StartZ=0 EndX=-60 EndY=35 EndZ=0
    g6: LineSegment StartX=-60 StartY=35 StartZ=0 EndX=-60 EndY=69 EndZ=0
    g7: LineSegment StartX=-60 StartY=69 StartZ=0 EndX=78 EndY=69 EndZ=0
    g8: LineSegment StartX=78 StartY=69 StartZ=0 EndX=78 EndY=0 EndZ=0
    g9: LineSegment StartX=78 StartY=0 StartZ=0 EndX=-78 EndY=0 EndZ=0
    g10: Circle CenterX=0 CenterY=34.5 CenterZ=0 NormalX=0 NormalY=0 NormalZ=1 AngleXU=0 Radius=22.5
    g11: LineSegment [constr] StartX=0 StartY=34.5 StartZ=0 EndX=0 EndY=0 EndZ=0
    g12: LineSegment [constr] StartX=0 StartY=34.5 StartZ=0 EndX=0 EndY=69 EndZ=0
  constraints (34):
    c: Coincident(g0,g1)
    c: Coincident(g1,g2)
    c: Coincident(g2,g3)
    c: Coincident(g3,g0)
    c: Horizontal(g2)
    c: Vertical(g1)
    c: Vertical(g3)
    c: PointOnObject(g0,g-1)
    c: Symmetric(g0,g0,g-2)
    c: DistanceX(g0,g0) = 156
    c: DistanceY(g3,g3) = 69
    c: Coincident(g0,g4)
    c: PointOnObject(g4,g3)
    c: Coincident(g4,g5)
    c: Horizontal(g5)
    c: Coincident(g5,g6)
    c: PointOnObject(g6,g2)
    c: Vertical(g6)
    c: Coincident(g6,g7)
    c: Coincident(g7,g1)
    c: Coincident(g7,g8)
    c: Coincident(g8,g0)
    c: Coincident(g8,g9)
    c: Coincident(g9,g4)
    c: DistanceY(g4,g4) = 35
    c: DistanceX(g5,g5) = 18
    c: PointOnObject(g10,g-2)
    c: Coincident(g11,g10)
    c: Coincident(g11,g-1)
    c: Coincident(g12,g10)
    c: PointOnObject(g12,g7)
    c: Vertical(g12)
    c: Equal(g12,g11)
    c: Diameter(g10) = 45
FEATURE [PartDesign::Pad] Pad009
  Direction = (0,-1,2e-16)
  Length = 18
  Length2 = 10
  Placement = pos=(0,0,0) rot=(1,0,0;1.5708rad)
  Profile = -> Sketch020
  ReferenceAxis = -> Sketch020 [N_Axis]
  Suppressed = false
  Type = 0
  expr: Length = <<Parameter>>.Brettdicke
FEATURE [PartDesign::Body] Body019  label="Einflugloch_45mm"
  AllowCompound = false
  Group = -> [Sketch020,Pad009]
  Origin = -> Origin019
  Placement = pos=(1374,-191,69) rot=(0.57735,-0.57735,0.57735;4.18879rad)
  Tip = -> Pad009
FEATURE [Sketcher::SketchObject] Sketch021
  ArcFitTolerance = 0
  AttachmentSupport = -> [XZ_Plane020]
  FullyConstrained = true
  MakeInternals = false
  MapMode = 5
  Placement = pos=(0,0,0) rot=(1,0,0;1.5708rad)
  expr: Constraints[25] = <<Parameter>>.Brettdicke
  sketch-geometry (13):
    g0: LineSegment [constr] StartX=-78 StartY=0 StartZ=0 EndX=78 EndY=0 EndZ=0
    g1: LineSegment [constr] StartX=78 StartY=0 StartZ=0 EndX=78 EndY=69 EndZ=0
    g2: LineSegment [constr] StartX=78 StartY=69 StartZ=0 EndX=-78 EndY=69 EndZ=0
    g3: LineSegment [constr] StartX=-78 StartY=69 StartZ=0 EndX=-78 EndY=0 EndZ=0
    g4: LineSegment StartX=-78 StartY=0 StartZ=0 EndX=-78 EndY=35 EndZ=0
    g5: LineSegment StartX=-78 StartY=35 StartZ=0 EndX=-60 EndY=35 EndZ=0
    g6: LineSegment StartX=-60 StartY=35 StartZ=0 EndX=-60 EndY=69 EndZ=0
    g7: LineSegment StartX=-60 StartY=69 StartZ=0 EndX=78 EndY=69 EndZ=0
    g8: LineSegment StartX=78 StartY=69 StartZ=0 EndX=78 EndY=0 EndZ=0
    g9: LineSegment StartX=78 StartY=0 StartZ=0 EndX=-78 EndY=0 EndZ=0
    g10: Circle CenterX=0 CenterY=34.5 CenterZ=0 NormalX=0 NormalY=0 NormalZ=1 AngleXU=0 Radius=16
    g11: LineSegment [constr] StartX=0 StartY=34.5 StartZ=0 EndX=0 EndY=0 EndZ=0
    g12: LineSegment [constr] StartX=0 StartY=34.5 StartZ=0 EndX=0 EndY=69 EndZ=0
  constraints (34):
    c: Coincident(g0,g1)
    c: Coincident(g1,g2)
    c: Coincident(g2,g3)
    c: Coincident(g3,g0)
    c: Horizontal(g2)
    c: Vertical(g1)
    c: Vertical(g3)
    c: PointOnObject(g0,g-1)
    c: Symmetric(g0,g0,g-2)
    c: DistanceX(g0,g0) = 156
    c: DistanceY(g3,g3) = 69
    c: Coincident(g0,g4)
    c: PointOnObject(g4,g3)
    c: Coincident(g4,g5)
    c: Horizontal(g5)
    c: Coincident(g5,g6)
    c: PointOnObject(g6,g2)
    c: Vertical(g6)
    c: Coincident(g6,g7)
    c: Coincident(g7,g1)
    c: Coincident(g7,g8)
    c: Coincident(g8,g0)
    c: Coincident(g8,g9)
    c: Coincident(g9,g4)
    c: DistanceY(g4,g4) = 35
    c: DistanceX(g5,g5) = 18
    c: PointOnObject(g10,g-2)
    c: Coincident(g11,g10)
    c: Coincident(g11,g-1)
    c: Coincident(g12,g10)
    c: PointOnObject(g12,g7)
    c: Vertical(g12)
    c: Equal(g12,g11)
    c: Diameter(g10) = 32
FEATURE [PartDesign::Pad] Pad010
  Direction = (0,-1,2e-16)
  Length = 18
  Length2 = 10
  Placement = pos=(0,0,0) rot=(1,0,0;1.5708rad)
  Profile = -> Sketch021
  ReferenceAxis = -> Sketch021 [N_Axis]
  Suppressed = false
  Type = 0
  expr: Length = <<Parameter>>.Brettdicke
FEATURE [PartDesign::Body] Body020  label="Einflugloch_32mm"
  AllowCompound = false
  Group = -> [Sketch021,Pad010]
  Origin = -> Origin020
  Placement = pos=(1301,-191,69) rot=(0.57735,-0.57735,0.57735;4.18879rad)
  Tip = -> Pad010
FEATURE [Sketcher::SketchObject] Sketch022
  ArcFitTolerance = 0
  AttachmentSupport = -> [XZ_Plane021]
  FullyConstrained = true
  MakeInternals = false
  MapMode = 5
  Placement = pos=(0,0,0) rot=(1,0,0;1.5708rad)
  expr: Constraints[25] = <<Parameter>>.Brettdicke
  sketch-geometry (13):
    g0: LineSegment [constr] StartX=-78 StartY=0 StartZ=0 EndX=78 EndY=0 EndZ=0
    g1: LineSegment [constr] StartX=78 StartY=0 StartZ=0 EndX=78 EndY=69 EndZ=0
    g2: LineSegment [constr] StartX=78 StartY=69 StartZ=0 EndX=-78 EndY=69 EndZ=0
    g3: LineSegment [constr] StartX=-78 StartY=69 StartZ=0 EndX=-78 EndY=0 EndZ=0
    g4: LineSegment StartX=-78 StartY=0 StartZ=0 EndX=-78 EndY=35 EndZ=0
    g5: LineSegment StartX=-78 StartY=35 StartZ=0 EndX=-60 EndY=35 EndZ=0
    g6: LineSegment StartX=-60 StartY=35 StartZ=0 EndX=-60 EndY=69 EndZ=0
    g7: LineSegment StartX=-60 StartY=69 StartZ=0 EndX=78 EndY=69 EndZ=0
    g8: LineSegment StartX=78 StartY=69 StartZ=0 EndX=78 EndY=0 EndZ=0
    g9: LineSegment StartX=78 StartY=0 StartZ=0 EndX=-78 EndY=0 EndZ=0
    g10: Circle CenterX=0 CenterY=34.5 CenterZ=0 NormalX=0 NormalY=0 NormalZ=1 AngleXU=0 Radius=13.5
    g11: LineSegment [constr] StartX=0 StartY=34.5 StartZ=0 EndX=0 EndY=0 EndZ=0
    g12: LineSegment [constr] StartX=0 StartY=34.5 StartZ=0 EndX=0 EndY=69 EndZ=0
  constraints (34):
    c: Coincident(g0,g1)
    c: Coincident(g1,g2)
    c: Coincident(g2,g3)
    c: Coincident(g3,g0)
    c: Horizontal(g2)
    c: Vertical(g1)
    c: Vertical(g3)
    c: PointOnObject(g0,g-1)
    c: Symmetric(g0,g0,g-2)
    c: DistanceX(g0,g0) = 156
    c: DistanceY(g3,g3) = 69
    c: Coincident(g0,g4)
    c: PointOnObject(g4,g3)
    c: Coincident(g4,g5)
    c: Horizontal(g5)
    c: Coincident(g5,g6)
    c: PointOnObject(g6,g2)
    c: Vertical(g6)
    c: Coincident(g6,g7)
    c: Coincident(g7,g1)
    c: Coincident(g7,g8)
    c: Coincident(g8,g0)
    c: Coincident(g8,g9)
    c: Coincident(g9,g4)
    c: DistanceY(g4,g4) = 35
    c: DistanceX(g5,g5) = 18
    c: PointOnObject(g10,g-2)
    c: Coincident(g11,g10)
    c: Coincident(g11,g-1)
    c: Coincident(g12,g10)
    c: PointOnObject(g12,g7)
    c: Vertical(g12)
    c: Equal(g12,g11)
    c: Diameter(g10) = 27
FEATURE [PartDesign::Pad] Pad011
  Direction = (0,-1,2e-16)
  Length = 18
  Length2 = 10
  Placement = pos=(0,0,0) rot=(1,0,0;1.5708rad)
  Profile = -> Sketch022
  ReferenceAxis = -> Sketch022 [N_Axis]
  Suppressed = false
  Type = 0
  expr: Length = <<Parameter>>.Brettdicke
FEATURE [PartDesign::Body] Body021  label="Einflugloch_27mm"
  AllowCompound = false
  Group = -> [Sketch022,Pad011]
  Origin = -> Origin021
  Placement = pos=(1228,-191,69) rot=(0.57735,-0.57735,0.57735;4.18879rad)
  Tip = -> Pad011
FEATURE [Part::Part2DObjectPython] Shape2DView  # Draft 2D object (typed FeaturePython)
  AutoUpdate = true
  Base = -> Body019
  Clip = false
  FuseArch = false
  HiddenLines = false
  InPlace = true
  OnlySolids = false
  Projection = (0,0,1)
  ProjectionMode = 0
  SegmentLength = 0.05
  Tessellation = false
  VisibleOnly = false
FEATURE [Part::Part2DObjectPython] Shape2DView008  # Draft 2D object (typed FeaturePython)
  AutoUpdate = true
  Base = -> Body020
  Clip = false
  FuseArch = false
  HiddenLines = false
  InPlace = true
  OnlySolids = false
  Projection = (0,0,1)
  ProjectionMode = 0
  SegmentLength = 0.05
  Tessellation = false
  VisibleOnly = false
FEATURE [Part::Part2DObjectPython] Shape2DView009  # Draft 2D object (typed FeaturePython)
  AutoUpdate = true
  Base = -> Body021
  Clip = false
  FuseArch = false
  HiddenLines = false
  InPlace = true
  OnlySolids = false
  Projection = (0,0,1)
  ProjectionMode = 0
  SegmentLength = 0.05
  Tessellation = false
  VisibleOnly = false
FEATURE [App::DocumentObjectGroup] Group004  label="Einfluglochscheiben"
  Group = -> [Body019,Body020,Body021,Shape2DView,Shape2DView008,Shape2DView009]
FEATURE [Sketcher::SketchObject] Sketch023
  ArcFitTolerance = 0
  AttachmentSupport = -> [XZ_Plane022]
  FullyConstrained = true
  MakeInternals = false
  MapMode = 5
  Placement = pos=(0,0,0) rot=(1,0,0;1.5708rad)
  sketch-geometry (10):
    g0: Circle CenterX=0 CenterY=0 CenterZ=0 NormalX=0 NormalY=0 NormalZ=1 AngleXU=0 Radius=2
    g1: LineSegment StartX=-9 StartY=8 StartZ=0 EndX=9 EndY=8 EndZ=0
    g2: LineSegment StartX=9 StartY=8 StartZ=0 EndX=9 EndY=-37 EndZ=0
    g3: LineSegment StartX=9 StartY=-37 StartZ=0 EndX=-9 EndY=-37 EndZ=0
    g4: LineSegment StartX=-9 StartY=-37 StartZ=0 EndX=-9 EndY=8 EndZ=0
    g5: LineSegment [constr] StartX=-9 StartY=10 StartZ=0 EndX=9 EndY=10 EndZ=0
    g6: LineSegment [constr] StartX=9 StartY=10 StartZ=0 EndX=9 EndY=-10 EndZ=0
    g7: LineSegment [constr] StartX=9 StartY=-10 StartZ=0 EndX=-9 EndY=-10 EndZ=0
    g8: LineSegment [constr] StartX=-9 StartY=-10 StartZ=0 EndX=-9 EndY=10 EndZ=0
    g9: LineSegment [constr] StartX=-9 StartY=0 StartZ=0 EndX=9 EndY=0 EndZ=0
  constraints (28):
    c: Coincident(g0,g-1)
    c: Diameter(g0) = 4
    c: Coincident(g1,g2)
    c: Coincident(g2,g3)
    c: Coincident(g3,g4)
    c: Coincident(g4,g1)
    c: Horizontal(g3)
    c: Vertical(g2)
    c: Vertical(g4)
    c: Symmetric(g1,g1,g-2)
    c: DistanceX(g1,g1) = 18
    c: Coincident(g5,g6)
    c: Coincident(g6,g7)
    c: Coincident(g7,g8)
    c: Coincident(g8,g5)
    c: Horizontal(g7)
    c: Vertical(g6)
    c: Vertical(g8)
    c: DistanceX(g5,g5) = 18
    c: DistanceY(g8,g8) = 20
    c: PointOnObject(g9,g8)
    c: PointOnObject(g9,g6)
    c: Horizontal(g9)
    c: DistanceY(g9,g5) = 10
    c: Symmetric(g5,g5,g-2)
    c: PointOnObject(g0,g9)
    c: DistanceY(g2,g2) = 45
    c: DistanceY(g-1,g1) = 8
FEATURE [PartDesign::Pad] Pad012
  Direction = (0,-1,2e-16)
  Length = 4
  Length2 = 10
  Placement = pos=(0,0,0) rot=(1,0,0;1.5708rad)
  Profile = -> Sketch023
  ReferenceAxis = -> Sketch023 [N_Axis]
  Suppressed = false
  Type = 0
FEATURE [PartDesign::Chamfer] Chamfer
  Angle = 45
  Base = -> Pad012 [Edge1,Edge2]
  BaseFeature = -> Pad012
  ChamferType = 0
  FlipDirection = false
  Placement = pos=(0,0,0) rot=(1,0,0;1.5708rad)
  Size = 4
  Size2 = 1
  SupportTransform = false
  Suppressed = false
  UseAllEdges = false
FEATURE [Sketcher::SketchObject] Sketch024
  ArcFitTolerance = 0
  AttachmentSupport = -> [YZ_Plane024]
  FullyConstrained = true
  MakeInternals = false
  MapMode = 5
  Placement = pos=(0,0,0) rot=(0.57735,0.57735,0.57735;2.0944rad)
  sketch-geometry (6):
    g0: LineSegment StartX=0 StartY=0 StartZ=0 EndX=-33 EndY=0 EndZ=0
    g1: LineSegment StartX=-33 StartY=0 StartZ=0 EndX=-33 EndY=-48 EndZ=0
    g2: LineSegment StartX=-33 StartY=-48 StartZ=0 EndX=-20 EndY=-48 EndZ=0
    g3: LineSegment StartX=-20 StartY=-48 StartZ=0 EndX=-20 EndY=-30 EndZ=0
    g4: LineSegment StartX=-20 StartY=-30 StartZ=0 EndX=0 EndY=-30 EndZ=0
    g5: LineSegment StartX=0 StartY=-30 StartZ=0 EndX=0 EndY=0 EndZ=0
  constraints (17):
    c: Coincident(g-1,g0)
    c: PointOnObject(g0,g-1)
    c: Coincident(g0,g1)
    c: Vertical(g1)
    c: Coincident(g1,g2)
    c: Horizontal(g2)
    c: Coincident(g2,g3)
    c: Vertical(g3)
    c: Coincident(g3,g4)
    c: PointOnObject(g4,g-2)
    c: Horizontal(g4)
    c: Coincident(g4,g5)
    c: Coincident(g5,g0)
    c: DistanceY(g1,g1) = 48
    c: DistanceX(g0,g0) = 33
    c: DistanceY(g3,g3) = 18
    c: DistanceX(g4,g4) = 20
FEATURE [PartDesign::Pad] Pad013
  Direction = (1,0,0)
  Length = 23
  Length2 = 10
  Midplane = true
  Placement = pos=(0,0,0) rot=(0.57735,0.57735,0.57735;2.0944rad)
  Profile = -> Sketch024
  ReferenceAxis = -> Sketch024 [N_Axis]
  Suppressed = false
  Type = 0
FEATURE [Sketcher::SketchObject] Sketch025
  ArcFitTolerance = 0
  AttachmentSupport = -> [XZ_Plane025]
  FullyConstrained = true
  MakeInternals = false
  MapMode = 5
  Placement = pos=(0,0,0) rot=(1,0,0;1.5708rad)
  sketch-geometry (4):
    g0: LineSegment StartX=-42.5 StartY=220 StartZ=0 EndX=42.5 EndY=220 EndZ=0
    g1: LineSegment StartX=42.5 StartY=220 StartZ=0 EndX=42.5 EndY=-220 EndZ=0
    g2: LineSegment StartX=42.5 StartY=-220 StartZ=0 EndX=-42.5 EndY=-220 EndZ=0
    g3: LineSegment StartX=-42.5 StartY=-220 StartZ=0 EndX=-42.5 EndY=220 EndZ=0
  constraints (10):
    c: Coincident(g0,g1)
    c: Coincident(g1,g2)
    c: Coincident(g2,g3)
    c: Coincident(g3,g0)
    c: Horizontal(g2)
    c: Vertical(g1)
    c: DistanceY(g1,g1) = 440
    c: Symmetric(g0,g2,g-1)
    c: DistanceX(g2,g2) = 85
    c: Symmetric(g0,g0,g-2)
FEATURE [PartDesign::Pad] Pad014
  Direction = (0,-1,2e-16)
  Length = 10
  Length2 = 10
  Placement = pos=(0,0,0) rot=(1,0,0;1.5708rad)
  Profile = -> Sketch025
  ReferenceAxis = -> Sketch025 [N_Axis]
  Reversed = true
  Suppressed = false
  Type = 0
FEATURE [PartDesign::Chamfer] Chamfer001
  Angle = 45
  Base = -> Chamfer [Edge18]
  BaseFeature = -> Chamfer
  ChamferType = 0
  FlipDirection = false
  Placement = pos=(0,0,0) rot=(1,0,0;1.5708rad)
  Refine = true
  Size = 1
  Size2 = 1
  SupportTransform = false
  Suppressed = false
  UseAllEdges = false
FEATURE [PartDesign::Body] Body022  label="Drehbarer_Halter"
  AllowCompound = false
  Group = -> [Sketch023,Pad012,Chamfer,Chamfer001]
  Origin = -> Origin022
  Placement = pos=(-69,-80,69) rot=(0,0,1;0rad)
  Tip = -> Chamfer001
FEATURE [PartDesign::FeatureBase] Clone009
  BaseFeature = -> Body022
  Placement = pos=(-69,-80,69) rot=(0,0,1;0rad)
  Suppressed = false
FEATURE [PartDesign::Body] Body023  label="Drehbarer_Halter001"
  AllowCompound = false
  BaseFeature = -> Body022
  Group = -> [Clone009]
  Origin = -> Origin023
  Placement = pos=(138,0,0) rot=(0,0,1;0rad)
  Tip = -> Clone009
FEATURE [Sketcher::SketchObject] Sketch026
  ArcFitTolerance = 0
  AttachmentSupport = -> [Pad013]
  FullyConstrained = true
  MakeInternals = false
  MapMode = 5
  Placement = pos=(-7.3e-15,-33,0) rot=(0.57735,0.57735,-0.57735;2.0944rad)
  sketch-geometry (2):
    g0: Circle CenterX=6 CenterY=0 CenterZ=0 NormalX=0 NormalY=0 NormalZ=1 AngleXU=0 Radius=2
    g1: Circle CenterX=23 CenterY=0 CenterZ=0 NormalX=0 NormalY=0 NormalZ=1 AngleXU=0 Radius=2
  constraints (6):
    c: PointOnObject(g0,g-1)
    c: PointOnObject(g1,g-1)
    c: Equal(g0,g1)
    c: Diameter(g0) = 4
    c: DistanceX(g-1,g0) = 6
    c: DistanceX(g0,g1) = 17
FEATURE [PartDesign::Pocket] Pocket007
  BaseFeature = -> Pad013
  Direction = (0,1,0)
  Length = 5
  Length2 = 5
  Placement = pos=(0,0,0) rot=(0.57735,0.57735,0.57735;2.0944rad)
  Profile = -> Sketch026
  ReferenceAxis = -> Sketch026 [N_Axis]
  Refine = true
  Suppressed = false
  Type = 1
FEATURE [Sketcher::SketchObject] Sketch027
  ArcFitTolerance = 0
  AttachmentSupport = -> [Pad008]
  FullyConstrained = true
  MakeInternals = false
  MapMode = 5
  Placement = pos=(0,-4,0) rot=(1,0,0;1.5708rad)
  sketch-geometry (2):
    g0: Circle CenterX=-69 CenterY=9 CenterZ=0 NormalX=0 NormalY=0 NormalZ=1 AngleXU=0 Radius=1.5
    g1: Circle CenterX=69 CenterY=9 CenterZ=0 NormalX=0 NormalY=0 NormalZ=1 AngleXU=0 Radius=1.5
  constraints (5):
    c: Symmetric(g0,g1,g-2)
    c: Equal(g0,g1)
    c: DistanceY(g-1,g0) = 9
    c: DistanceX(g0,g-1) = 69
    c: Diameter(g0) = 3
FEATURE [PartDesign::Pocket] Pocket008
  BaseFeature = -> Pad008
  Direction = (0,1,-2e-16)
  Length = 5
  Length2 = 5
  Placement = pos=(0,0,0) rot=(1,0,0;1.5708rad)
  Profile = -> Sketch027
  ReferenceAxis = -> Sketch027 [N_Axis]
  Refine = true
  Suppressed = false
  Type = 1
FEATURE [Sketcher::SketchObject] Sketch028
  ArcFitTolerance = 0
  AttachmentSupport = -> [Pad007]
  FullyConstrained = true
  MakeInternals = false
  MapMode = 5
  Placement = pos=(0,0,5) rot=(0,0,1;0rad)
  sketch-geometry (4):
    g0: Circle CenterX=-69 CenterY=60 CenterZ=0 NormalX=0 NormalY=0 NormalZ=1 AngleXU=0 Radius=1.5
    g1: Circle CenterX=69 CenterY=60 CenterZ=0 NormalX=0 NormalY=0 NormalZ=1 AngleXU=0 Radius=1.5
    g2: Circle CenterX=-69 CenterY=-60 CenterZ=0 NormalX=0 NormalY=0 NormalZ=1 AngleXU=0 Radius=1.5
    g3: Circle CenterX=69 CenterY=-60 CenterZ=0 NormalX=0 NormalY=0 NormalZ=1 AngleXU=0 Radius=1.5
  constraints (9):
    c: Equal(g0,g1)
    c: Equal(g1,g2)
    c: Equal(g2,g3)
    c: Symmetric(g0,g1,g-2)
    c: Symmetric(g2,g3,g-2)
    c: Symmetric(g2,g0,g-1)
    c: Diameter(g0) = 3
    c: DistanceY(g-1,g0) = 60
    c: DistanceX(g0,g-1) = 69
FEATURE [PartDesign::Pocket] Pocket009
  BaseFeature = -> Pad007
  Direction = (0,0,-1)
  Length = 5
  Length2 = 5
  Profile = -> Sketch028
  ReferenceAxis = -> Sketch028 [N_Axis]
  Refine = true
  Suppressed = false
  Type = 1
FEATURE [PartDesign::Chamfer] Chamfer003
  Angle = 45
  Base = -> Pocket009 [Edge19,Edge20,Edge17,Edge18]
  BaseFeature = -> Pocket009
  ChamferType = 0
  FlipDirection = false
  Refine = true
  Size = 1
  Size2 = 1
  SupportTransform = false
  Suppressed = false
  UseAllEdges = false
FEATURE [PartDesign::Body] Body009  label="Dach"
  AllowCompound = false
  Group = -> [Sketch009,Pad007,Sketch028,Pocket009,Chamfer003]
  Origin = -> Origin009
  Placement = pos=(0,-25.118,254.583) rot=(1,0,0;0.305433rad)
  Tip = -> Chamfer003
FEATURE [Sketcher::SketchObject] Sketch029
  ArcFitTolerance = 0
  AttachmentSupport = -> [Pad014]
  FullyConstrained = true
  MakeInternals = false
  MapMode = 5
  Placement = pos=(0,10,0) rot=(-1,0,0;1.5708rad)
  sketch-geometry (6):
    g0: Circle CenterX=22.5 CenterY=-110 CenterZ=0 NormalX=0 NormalY=0 NormalZ=1 AngleXU=0 Radius=2
    g1: Circle CenterX=-22.5 CenterY=-110 CenterZ=0 NormalX=0 NormalY=0 NormalZ=1 AngleXU=0 Radius=2
    g2: Circle CenterX=22.5 CenterY=110 CenterZ=0 NormalX=0 NormalY=0 NormalZ=1 AngleXU=0 Radius=2
    g3: Circle CenterX=-22.5 CenterY=110 CenterZ=0 NormalX=0 NormalY=0 NormalZ=1 AngleXU=0 Radius=2
    g4: Circle CenterX=0 CenterY=-197 CenterZ=0 NormalX=0 NormalY=0 NormalZ=1 AngleXU=0 Radius=2.25
    g5: Circle CenterX=0 CenterY=197 CenterZ=0 NormalX=0 NormalY=0 NormalZ=1 AngleXU=0 Radius=2.25
  constraints (14):
    c: Equal(g2,g0)
    c: Equal(g0,g1)
    c: Equal(g1,g3)
    c: Diameter(g0) = 4
    c: Symmetric(g0,g1,g-2)
    c: Symmetric(g2,g3,g-2)
    c: Symmetric(g2,g0,g-1)
    c: DistanceX(g-1,g0) = 22.5
    c: Distance(g0,g-1) = 110
    c: PointOnObject(g4,g-2)
    c: Equal(g5,g4)
    c: Symmetric(g4,g5,g-1)
    c: Distance(g4,g-1) = 197
    c: Diameter(g4) = 4.5
FEATURE [PartDesign::Pocket] Pocket010
  BaseFeature = -> Pad014
  Direction = (0,-1,-2e-16)
  Length = 5
  Length2 = 5
  Placement = pos=(0,0,0) rot=(1,0,0;1.5708rad)
  Profile = -> Sketch029
  ReferenceAxis = -> Sketch029 [N_Axis]
  Refine = true
  Suppressed = false
  Type = 1
FEATURE [PartDesign::Chamfer] Chamfer004
  Angle = 45
  Base = -> Pocket010 [Edge24,Edge21,Edge19,Edge23]
  BaseFeature = -> Pocket010
  ChamferType = 0
  FlipDirection = false
  Placement = pos=(0,0,0) rot=(1,0,0;1.5708rad)
  Refine = true
  Size = 1
  Size2 = 1
  SupportTransform = false
  Suppressed = false
  UseAllEdges = false
FEATURE [PartDesign::Body] Body025  label="Brett_Rückseite_Plastik"
  AllowCompound = false
  Group = -> [Sketch025,Pad014,Sketch029,Pocket010,Chamfer004]
  Origin = -> Origin025
  Placement = pos=(0,80,137) rot=(0,0,1;0rad)
  Tip = -> Chamfer004
FEATURE [Part::FeaturePython] Screw  label="#8x1 1/4in-Schraube"  # WARN: FeaturePython — macro-defined, semantics opaque (R4)
  BaseObject = -> Body004 [Pocket006.Edge34]
  Diameter = 9
  Invert = true
  LeftHanded = false
  Length = 5
  LengthCustom = 31.75
  MatchOuter = false
  Offset = 1
  OffsetAngle = 0
  Placement = pos=(79,-57,-9) rot=(0,1,0;1.5708rad)
  Thread = false
  Type = 15
FEATURE [Part::FeaturePython] Screw001  label="#8x1 1/4in-Schraube006"  # WARN: FeaturePython — macro-defined, semantics opaque (R4)
  BaseObject = -> Body004 [Pocket006.Edge33]
  Diameter = 9
  Invert = true
  LeftHanded = false
  Length = 5
  LengthCustom = 31.75
  MatchOuter = false
  Offset = 1
  OffsetAngle = 0
  Placement = pos=(79,57,-9) rot=(0,1,0;1.5708rad)
  Thread = false
  Type = 15
FEATURE [Part::FeaturePython] Screw002  label="#8x1 1/4in-Schraube007"  # WARN: FeaturePython — macro-defined, semantics opaque (R4)
  BaseObject = -> Body003 [Pocket005.Edge59]
  Diameter = 9
  Invert = false
  LeftHanded = false
  Length = 5
  LengthCustom = 31.75
  MatchOuter = false
  Offset = 1
  OffsetAngle = 0
  Placement = pos=(-79,57,-9) rot=(0,-1,0;1.5708rad)
  Thread = false
  Type = 15
FEATURE [Part::FeaturePython] Screw003  label="#8x1 1/4in-Schraube008"  # WARN: FeaturePython — macro-defined, semantics opaque (R4)
  BaseObject = -> Body003 [Pocket005.Edge60]
  Diameter = 9
  Invert = false
  LeftHanded = false
  Length = 5
  LengthCustom = 31.75
  MatchOuter = false
  Offset = 1
  OffsetAngle = 0
  Placement = pos=(-79,-57,-9) rot=(0,-1,0;1.5708rad)
  Thread = false
  Type = 15
FEATURE [Part::FeaturePython] Screw004  label="#8x1 1/4in-Schraube009"  # WARN: FeaturePython — macro-defined, semantics opaque (R4)
  BaseObject = -> Body002 [Pocket004.Edge32]
  Diameter = 9
  Invert = false
  LeftHanded = false
  Length = 5
  LengthCustom = 31.75
  MatchOuter = false
  Offset = 1
  OffsetAngle = 0
  Placement = pos=(69,81,142) rot=(-1,0,0;1.5708rad)
  Thread = false
  Type = 15
FEATURE [Part::FeaturePython] Screw005  label="#8x1 1/4in-Schraube010"  # WARN: FeaturePython — macro-defined, semantics opaque (R4)
  BaseObject = -> Body002 [Pocket004.Edge31]
  Diameter = 9
  Invert = false
  LeftHanded = false
  Length = 5
  LengthCustom = 31.75
  MatchOuter = false
  Offset = 1
  OffsetAngle = 0
  Placement = pos=(-69,81,142) rot=(-1,0,0;1.5708rad)
  Thread = false
  Type = 15
FEATURE [PartDesign::Chamfer] Chamfer005
  Angle = 45
  Base = -> Pocket008 [Edge15,Edge16]
  BaseFeature = -> Pocket008
  ChamferType = 0
  FlipDirection = false
  Placement = pos=(0,0,0) rot=(1,0,0;1.5708rad)
  Refine = true
  Size = 1
  Size2 = 1
  SupportTransform = false
  Suppressed = false
  UseAllEdges = false
FEATURE [PartDesign::Body] Body018  label="Frontplatte_Plastik"
  AllowCompound = false
  Group = -> [Sketch011,Pad008,Sketch027,Pocket008,Chamfer005]
  Origin = -> Origin018
  Placement = pos=(0,-113,122) rot=(0,0,1;0rad)
  Tip = -> Chamfer005
FEATURE [Part::FeaturePython] Screw006  label="#6x1in-Schraube"  # WARN: FeaturePython — macro-defined, semantics opaque (R4)
  BaseObject = -> Body018 [Chamfer005.Edge1]
  Diameter = 7
  Invert = false
  LeftHanded = false
  Length = 5
  LengthCustom = 25.4
  MatchOuter = false
  Offset = 1
  OffsetAngle = 0
  Placement = pos=(-69,-118,131) rot=(1,0,0;1.5708rad)
  Thread = false
  Type = 15
FEATURE [Part::FeaturePython] Screw007  label="#6x1in-Schraube023"  # WARN: FeaturePython — macro-defined, semantics opaque (R4)
  BaseObject = -> Body018 [Chamfer005.Edge6]
  Diameter = 7
  Invert = false
  LeftHanded = false
  Length = 5
  LengthCustom = 25.4
  MatchOuter = false
  Offset = 1
  OffsetAngle = 0
  Placement = pos=(69,-118,131) rot=(1,0,0;1.5708rad)
  Thread = false
  Type = 15
FEATURE [Part::FeaturePython] Screw008  label="#6x1in-Schraube009"  # WARN: FeaturePython — macro-defined, semantics opaque (R4)
  BaseObject = -> Body022 [Chamfer001.Edge1]
  Diameter = 7
  Invert = false
  LeftHanded = false
  Length = 5
  LengthCustom = 25.4
  MatchOuter = false
  Offset = 1
  OffsetAngle = 0
  Placement = pos=(-69,-85,69) rot=(1,0,0;1.5708rad)
  Thread = false
  Type = 15
FEATURE [Part::FeaturePython] Screw009  label="#6x1in-Schraube010"  # WARN: FeaturePython — macro-defined, semantics opaque (R4)
  BaseObject = -> Body023 [Clone009.Edge1]
  Diameter = 7
  Invert = false
  LeftHanded = false
  Length = 5
  LengthCustom = 25.4
  MatchOuter = false
  Offset = 1
  OffsetAngle = 0
  Placement = pos=(69,-85,69) rot=(1,0,0;1.5708rad)
  Thread = false
  Type = 15
FEATURE [Part::FeaturePython] Screw010  label="#6x1in-Schraube011"  # WARN: FeaturePython — macro-defined, semantics opaque (R4)
  BaseObject = -> Body009 [Chamfer003.Edge7]
  Diameter = 7
  Invert = false
  LeftHanded = false
  Length = 5
  LengthCustom = 25.4
  MatchOuter = false
  Offset = 1
  OffsetAngle = 0
  Placement = pos=(-69,-84.1453,242.263) rot=(1,0,0;0.305433rad)
  Thread = false
  Type = 15
FEATURE [Part::FeaturePython] Screw011  label="#6x1in-Schraube012"  # WARN: FeaturePython — macro-defined, semantics opaque (R4)
  BaseObject = -> Body009 [Chamfer003.Edge8]
  Diameter = 7
  Invert = false
  LeftHanded = false
  Length = 5
  LengthCustom = 25.4
  MatchOuter = false
  Offset = 1
  OffsetAngle = 0
  Placement = pos=(69,-84.1453,242.263) rot=(1,0,0;0.305433rad)
  Thread = false
  Type = 15
FEATURE [Part::FeaturePython] Screw012  label="#6x1in-Schraube013"  # WARN: FeaturePython — macro-defined, semantics opaque (R4)
  BaseObject = -> Body009 [Chamfer003.Edge1]
  Diameter = 7
  Invert = false
  LeftHanded = false
  Length = 5
  LengthCustom = 25.4
  MatchOuter = false
  Offset = 1
  OffsetAngle = 0
  Placement = pos=(-69,30.3008,278.348) rot=(1,0,0;0.305433rad)
  Thread = false
  Type = 15
FEATURE [Part::FeaturePython] Screw013  label="#6x1in-Schraube014"  # WARN: FeaturePython — macro-defined, semantics opaque (R4)
  BaseObject = -> Body009 [Chamfer003.Edge6]
  Diameter = 7
  Invert = false
  LeftHanded = false
  Length = 5
  LengthCustom = 25.4
  MatchOuter = false
  Offset = 1
  OffsetAngle = 0
  Placement = pos=(69,30.3008,278.348) rot=(1,0,0;0.305433rad)
  Thread = false
  Type = 15
FEATURE [Part::FeaturePython] Screw014  label="#6x1in-Schraube019"  # WARN: FeaturePython — macro-defined, semantics opaque (R4)
  BaseObject = -> Body025 [Chamfer004.Edge1]
  Diameter = 7
  Invert = false
  LeftHanded = false
  Length = 5
  LengthCustom = 25.4
  MatchOuter = false
  Offset = 1
  OffsetAngle = 0
  Placement = pos=(22.5,91,247) rot=(-1,0,0;1.5708rad)
  Thread = false
  Type = 15
FEATURE [Part::FeaturePython] Screw015  label="#6x1in-Schraube020"  # WARN: FeaturePython — macro-defined, semantics opaque (R4)
  BaseObject = -> Body025 [Chamfer004.Edge8]
  Diameter = 7
  Invert = false
  LeftHanded = false
  Length = 5
  LengthCustom = 25.4
  MatchOuter = false
  Offset = 1
  OffsetAngle = 0
  Placement = pos=(-22.5,91,247) rot=(-1,0,0;1.5708rad)
  Thread = false
  Type = 15
FEATURE [Part::FeaturePython] Screw016  label="#6x1in-Schraube021"  # WARN: FeaturePython — macro-defined, semantics opaque (R4)
  BaseObject = -> Body025 [Chamfer004.Edge9]
  Diameter = 7
  Invert = false
  LeftHanded = false
  Length = 5
  LengthCustom = 25.4
  MatchOuter = false
  Offset = 1
  OffsetAngle = 0
  Placement = pos=(-22.5,91,27) rot=(-1,0,0;1.5708rad)
  Thread = false
  Type = 15
FEATURE [Part::FeaturePython] Screw017  label="#6x1in-Schraube022"  # WARN: FeaturePython — macro-defined, semantics opaque (R4)
  BaseObject = -> Body025 [Chamfer004.Edge10]
  Diameter = 7
  Invert = false
  LeftHanded = false
  Length = 5
  LengthCustom = 25.4
  MatchOuter = false
  Offset = 1
  OffsetAngle = 0
  Placement = pos=(22.5,91,27) rot=(-1,0,0;1.5708rad)
  Thread = false
  Type = 15
FEATURE [PartDesign::Fillet] Fillet
  Base = -> Pocket007 [Edge21]
  BaseFeature = -> Pocket007
  Placement = pos=(0,0,0) rot=(0.57735,0.57735,0.57735;2.0944rad)
  Radius = 12
  Refine = true
  SupportTransform = false
  Suppressed = false
  UseAllEdges = false
FEATURE [PartDesign::Chamfer] Chamfer006
  Angle = 45
  Base = -> Fillet [Edge19,Edge20]
  BaseFeature = -> Fillet
  ChamferType = 0
  FlipDirection = false
  Placement = pos=(0,0,0) rot=(0.57735,0.57735,0.57735;2.0944rad)
  Refine = true
  Size = 2
  Size2 = 1
  SupportTransform = false
  Suppressed = false
  UseAllEdges = false
FEATURE [PartDesign::Body] Body024  label="Griff"
  AllowCompound = false
  Group = -> [Sketch024,Pad013,Sketch026,Pocket007,Fillet,Chamfer006]
  Origin = -> Origin024
  Placement = pos=(0,-80,80) rot=(0,0,1;0rad)
  Tip = -> Chamfer006
FEATURE [App::DocumentObjectGroup] Group  label="Tür"
  Group = -> [Body008,Body024]
FEATURE [Part::FeaturePython] Screw018  label="#8x1 1/2in-Schraube"  # WARN: FeaturePython — macro-defined, semantics opaque (R4)
  BaseObject = -> Body024 [Chamfer006.Edge1]
  Diameter = 9
  Invert = false
  LeftHanded = false
  Length = 6
  LengthCustom = 38.1
  MatchOuter = false
  OffsetAngle = 0
  Placement = pos=(-4.7e-15,-113,74) rot=(1,0,0;1.5708rad)
  Thread = false
  Type = 15
FEATURE [Part::FeaturePython] Screw019  label="#8x1 1/2in-Schraube001"  # WARN: FeaturePython — macro-defined, semantics opaque (R4)
  BaseObject = -> Body024 [Chamfer006.Edge6]
  Diameter = 9
  Invert = false
  LeftHanded = false
  Length = 6
  LengthCustom = 38.1
  MatchOuter = false
  OffsetAngle = 0
  Placement = pos=(8e-16,-113,57) rot=(1,0,0;1.5708rad)
  Thread = false
  Type = 15
FEATURE [App::DocumentObjectGroup] Group005  label="Schrauben"
  Group = -> [Screw,Screw001,Screw002,Screw003,Screw004,Screw005,Screw006,Screw007,Screw008,Screw009,Screw010,Screw011,Screw012,Screw013,Screw014,Screw015,Screw016,Screw017,Screw018,Screw019]
FEATURE [TechDraw::DrawSVGTemplate] Template  label="Vorlage"
  Height = 297
  Orientation = 0
  Template = C:/Program Files/FreeCAD 1.0/data/Mod/TechDraw/Templates/A4_Portrait_blank.svg
  Width = 210
FEATURE [TechDraw::DrawProjGroupItem] View  label="Front"
  CoarseView = false
  Direction = (0,-1,0)
  Focus = 100
  HardHidden = false
  IsoCount = 0
  IsoHidden = false
  IsoVisible = false
  LockPosition = true
  Perspective = false
  Rotation = 0
  RotationVector = (1,0,0)
  ScaleType = 2
  ScrubCount = 1
  SeamHidden = false
  SeamVisible = false
  SmoothHidden = false
  SmoothVisible = true
  Source = -> [Body018]
  Type = 0
  X = 0
  XDirection = (1,0,0)
  Y = 0
FEATURE [TechDraw::DrawProjGroupItem] ProjItem  label="Links001"
  CoarseView = false
  Direction = (-1,-1e-16,0)
  Focus = 100
  HardHidden = false
  IsoCount = 0
  IsoHidden = false
  IsoVisible = false
  LockPosition = false
  Perspective = false
  Rotation = 0
  RotationVector = (1,0,0)
  ScaleType = 0
  ScrubCount = 1
  SeamHidden = false
  SeamVisible = false
  SmoothHidden = false
  SmoothVisible = true
  Source = -> [Body018]
  Type = 1
  X = 95
  XDirection = (1e-16,-1,0)
  Y = 0
FEATURE [TechDraw::DrawViewDimension] Dimension  label="Maß"
  AngleOverride = false
  Arbitrary = false
  ArbitraryTolerances = false
  BoxCorners = (2) [(-78,-22.5,0),(78,22.5,0)]
  EqualTolerance = true
  ExtensionAngle = 0
  FormatSpec = %.2w
  FormatSpecOverTolerance = %+.2w
  FormatSpecUnderTolerance = %+.2w
  Inverted = false
  LineAngle = 0
  LockPosition = false
  MeasureType = 1
  OverTolerance = 0
  References2D = -> [View]
  Rotation = 0
  ScaleType = 0
  TheoreticalExact = false
  Type = 1
  UnderTolerance = 0
  X = 0
  Y = 38.8303
FEATURE [TechDraw::DrawViewDimension] Dimension001  label="Maß001"
  AngleOverride = false
  Arbitrary = false
  ArbitraryTolerances = false
  BoxCorners = (2) [(-78,-22.5,0),(78,22.5,0)]
  EqualTolerance = true
  ExtensionAngle = 0
  FormatSpec = %.2w
  FormatSpecOverTolerance = %+.2w
  FormatSpecUnderTolerance = %+.2w
  Inverted = false
  LineAngle = 0
  LockPosition = false
  MeasureType = 1
  OverTolerance = 0
  References2D = -> [View]
  Rotation = 0
  ScaleType = 0
  TheoreticalExact = false
  Type = 2
  UnderTolerance = 0
  X = -94.7522
  Y = 0
FEATURE [TechDraw::DrawViewDimension] Dimension002  label="Maß002"
  AngleOverride = false
  Arbitrary = false
  ArbitraryTolerances = false
  BoxCorners = (2) [(-2,-22.5,0),(2,22.5,0)]
  EqualTolerance = true
  ExtensionAngle = 0
  FormatSpec = %.2w
  FormatSpecOverTolerance = %+.2w
  FormatSpecUnderTolerance = %+.2w
  Inverted = false
  LineAngle = 0
  LockPosition = false
  MeasureType = 1
  OverTolerance = 0
  References2D = -> [ProjItem]
  Rotation = 0
  ScaleType = 0
  TheoreticalExact = false
  Type = 1
  UnderTolerance = 0
  X = 0
  Y = 39.0082
FEATURE [TechDraw::DrawViewDimension] Dimension003  label="Maß003"
  AngleOverride = false
  Arbitrary = false
  ArbitraryTolerances = false
  BoxCorners = (2) [(-78,-22.5,0),(78,22.5,0)]
  EqualTolerance = true
  ExtensionAngle = 0
  FormatSpec = %.2w
  FormatSpecOverTolerance = %+.2w
  FormatSpecUnderTolerance = %+.2w
  Inverted = false
  LineAngle = 0
  LockPosition = false
  MeasureType = 1
  OverTolerance = 0
  References2D = -> [View]
  Rotation = 0
  ScaleType = 0
  TheoreticalExact = false
  Type = 0
  UnderTolerance = 0
  X = -73.5
  Y = -47.4635
FEATURE [TechDraw::DrawViewDimension] Dimension004  label="Maß004"
  AngleOverride = false
  Arbitrary = false
  ArbitraryTolerances = false
  BoxCorners = (2) [(-78,-22.5,0),(78,22.5,0)]
  EqualTolerance = true
  ExtensionAngle = 0
  FormatSpec = %.2w
  FormatSpecOverTolerance = %+.2w
  FormatSpecUnderTolerance = %+.2w
  Inverted = false
  LineAngle = 0
  LockPosition = false
  MeasureType = 1
  OverTolerance = 0
  References2D = -> [View]
  Rotation = 0
  ScaleType = 0
  TheoreticalExact = false
  Type = 0
  UnderTolerance = 0
  X = -86.2764
  Y = -18
FEATURE [TechDraw::DrawViewAnnotation] Annotation  label="Beschriftung"
  Font = osifont
  LineSpace = 100
  LockPosition = false
  MaxWidth = -1
  Rotation = 0
  ScaleType = 0
  Text = Plattendicke | ca. 4 bis 5 mm
  TextSize = 5
  TextStyle = 0
  X = 184.783
  Y = 252.125
FEATURE [TechDraw::DrawViewAnnotation] Annotation001  label="Beschriftung001"
  Font = osifont
  LineSpace = 100
  LockPosition = false
  MaxWidth = -1
  Rotation = 0
  ScaleType = 0
  Text = Frontplatte Plastik
  TextSize = 5
  TextStyle = 0
  X = 105.469
  Y = 277.5
FEATURE [TechDraw::DrawSVGTemplate] Template001  label="Vorlage001"
  Height = 297
  Orientation = 0
  Template = C:/Program Files/FreeCAD 1.0/data/Mod/TechDraw/Templates/A4_Portrait_blank.svg
  Width = 210
FEATURE [TechDraw::DrawProjGroupItem] View001  label="Front001"
  CoarseView = false
  Direction = (0,-1,0)
  Focus = 100
  HardHidden = false
  IsoCount = 0
  IsoHidden = false
  IsoVisible = false
  LockPosition = true
  Perspective = false
  Rotation = 0
  RotationVector = (1,0,0)
  ScaleType = 2
  ScrubCount = 1
  SeamHidden = false
  SeamVisible = false
  SmoothHidden = false
  SmoothVisible = true
  Source = -> [Body022]
  Type = 0
  X = 0
  XDirection = (1,0,0)
  Y = 0
FEATURE [TechDraw::DrawProjGroupItem] ProjItem001  label="Links002"
  CoarseView = false
  Direction = (-1,-1e-16,0)
  Focus = 100
  HardHidden = false
  IsoCount = 0
  IsoHidden = false
  IsoVisible = false
  LockPosition = false
  Perspective = false
  Rotation = 0
  RotationVector = (1,0,0)
  ScaleType = 0
  ScrubCount = 1
  SeamHidden = false
  SeamVisible = false
  SmoothHidden = false
  SmoothVisible = true
  Source = -> [Body022]
  Type = 1
  X = 26
  XDirection = (1e-16,-1,0)
  Y = 0
FEATURE [TechDraw::DrawViewDimension] Dimension005  label="Maß005"
  AngleOverride = false
  Arbitrary = false
  ArbitraryTolerances = false
  BoxCorners = (2) [(-9,-22.5,0),(9,22.5,0)]
  EqualTolerance = true
  ExtensionAngle = 0
  FormatSpec = %.2w
  FormatSpecOverTolerance = %+.2w
  FormatSpecUnderTolerance = %+.2w
  Inverted = false
  LineAngle = 0
  LockPosition = false
  MeasureType = 1
  OverTolerance = 0
  References2D = -> [View001]
  Rotation = 0
  ScaleType = 0
  TheoreticalExact = false
  Type = 1
  UnderTolerance = 0
  X = 0
  Y = -51.846
FEATURE [TechDraw::DrawViewDimension] Dimension006  label="Maß006"
  AngleOverride = false
  Arbitrary = false
  ArbitraryTolerances = false
  BoxCorners = (2) [(-9,-22.5,0),(9,22.5,0)]
  EqualTolerance = true
  ExtensionAngle = 0
  FormatSpec = %.2w
  FormatSpecOverTolerance = %+.2w
  FormatSpecUnderTolerance = %+.2w
  Inverted = false
  LineAngle = 0
  LockPosition = false
  MeasureType = 1
  OverTolerance = 0
  References2D = -> [View001]
  Rotation = 0
  ScaleType = 0
  TheoreticalExact = false
  Type = 0
  UnderTolerance = 0
  X = -36.1935
  Y = 0
FEATURE [TechDraw::DrawViewDimension] Dimension007  label="Maß007"
  AngleOverride = false
  Arbitrary = false
  ArbitraryTolerances = false
  BoxCorners = (2) [(-9,-22.5,0),(9,22.5,0)]
  EqualTolerance = true
  ExtensionAngle = 0
  FormatSpec = %.2w
  FormatSpecOverTolerance = %+.2w
  FormatSpecUnderTolerance = %+.2w
  Inverted = false
  LineAngle = 0
  LockPosition = false
  MeasureType = 1
  OverTolerance = 0
  References2D = -> [View001]
  Rotation = 0
  ScaleType = 0
  TheoreticalExact = false
  Type = 0
  UnderTolerance = 0
  X = -21.1165
  Y = 18.5
FEATURE [TechDraw::DrawViewDimension] Dimension008  label="Maß008"
  AngleOverride = false
  Arbitrary = false
  ArbitraryTolerances = false
  BoxCorners = (2) [(-2,-22.5,0),(2,22.5,0)]
  EqualTolerance = true
  ExtensionAngle = 0
  FormatSpec = %.2w
  FormatSpecOverTolerance = %+.2w
  FormatSpecUnderTolerance = %+.2w
  Inverted = false
  LineAngle = 0
  LockPosition = false
  MeasureType = 1
  OverTolerance = 0
  References2D = -> [ProjItem001]
  Rotation = 0
  ScaleType = 0
  TheoreticalExact = false
  Type = 1
  UnderTolerance = 0
  X = 0
  Y = 42.902
FEATURE [TechDraw::DrawViewAnnotation] Annotation002  label="Beschriftung002"
  Font = osifont
  LineSpace = 100
  LockPosition = false
  MaxWidth = -1
  Rotation = 0
  ScaleType = 0
  Text = Plattendicke | ca. 4 bis 5 mm
  TextSize = 5
  TextStyle = 0
  X = 134.374
  Y = 225.94
FEATURE [TechDraw::DrawViewAnnotation] Annotation003  label="Beschriftung003"
  Font = osifont
  LineSpace = 100
  LockPosition = false
  MaxWidth = -1
  Rotation = 0
  ScaleType = 0
  Text = Bohrung mittig | ansenken
  TextSize = 5
  TextStyle = 0
  X = 105
  Y = 184.5
FEATURE [TechDraw::DrawViewAnnotation] Annotation004  label="Beschriftung004"
  Font = osifont
  LineSpace = 100
  LockPosition = false
  MaxWidth = -1
  Rotation = 0
  ScaleType = 0
  Text = Drehbarer Halter Plastik
  TextSize = 5
  TextStyle = 0
  X = 105
  Y = 266.5
FEATURE [TechDraw::DrawViewAnnotation] Annotation005  label="Beschriftung005"
  Font = osifont
  LineSpace = 100
  LockPosition = false
  MaxWidth = -1
  Rotation = 0
  ScaleType = 0
  Text = Bohrungen ansenken
  TextSize = 5
  TextStyle = 0
  X = 69.2219
  Y = 147.106
FEATURE [TechDraw::DrawProjGroupItem] ProjItem002  label="VorneObenRechts"
  CoarseView = false
  Direction = (0.57735,-0.57735,0.57735)
  Focus = 100
  HardHidden = false
  IsoCount = 0
  IsoHidden = false
  IsoVisible = false
  LockPosition = false
  Perspective = false
  Rotation = 0
  RotationVector = (1,0,0)
  ScaleType = 0
  ScrubCount = 1
  SeamHidden = false
  SeamVisible = false
  SmoothHidden = false
  SmoothVisible = true
  Source = -> [Body018]
  Type = 7
  X = -5.96415
  XDirection = (0.707107,0.707107,0)
  Y = -122.982
FEATURE [TechDraw::DrawProjGroup] ProjGroup
  Anchor = -> View
  AutoDistribute = false
  LockPosition = false
  ProjectionType = 0
  Rotation = 0
  ScaleType = 0
  Source = -> [Body018]
  Views = -> [View,ProjItem,ProjItem002]
  X = 104.103
  Y = 192.304
  spacingX = 15
  spacingY = 15
FEATURE [TechDraw::DrawProjGroupItem] ProjItem003  label="VorneObenRechts001"
  CoarseView = false
  Direction = (0.57735,-0.57735,0.57735)
  Focus = 100
  HardHidden = false
  IsoCount = 0
  IsoHidden = false
  IsoVisible = false
  LockPosition = false
  Perspective = false
  Rotation = 0
  RotationVector = (1,0,0)
  ScaleType = 0
  ScrubCount = 1
  SeamHidden = false
  SeamVisible = false
  SmoothHidden = false
  SmoothVisible = true
  Source = -> [Body022]
  Type = 7
  X = 1.89205
  XDirection = (0.707107,0.707107,0)
  Y = -90.1547
FEATURE [TechDraw::DrawProjGroup] ProjGroup001
  Anchor = -> View001
  AutoDistribute = false
  LockPosition = false
  ProjectionType = 0
  Rotation = 0
  ScaleType = 0
  Source = -> [Body022]
  Views = -> [View001,ProjItem001,ProjItem003]
  X = 105
  Y = 148.5
  spacingX = 15
  spacingY = 15
FEATURE [TechDraw::DrawSVGTemplate] Template002  label="Vorlage002"
  Height = 297
  Orientation = 0
  Template = C:/Program Files/FreeCAD 1.0/data/Mod/TechDraw/Templates/A4_Portrait_blank.svg
  Width = 210
FEATURE [TechDraw::DrawProjGroupItem] View002  label="Front002"
  CoarseView = false
  Direction = (0,-1,0)
  Focus = 100
  HardHidden = false
  IsoCount = 0
  IsoHidden = false
  IsoVisible = false
  LockPosition = true
  Perspective = false
  Rotation = 0
  RotationVector = (1,0,0)
  ScaleType = 2
  ScrubCount = 1
  SeamHidden = false
  SeamVisible = false
  SmoothHidden = false
  SmoothVisible = true
  Source = -> [Body024]
  Type = 0
  X = 0
  XDirection = (1,0,0)
  Y = 0
FEATURE [TechDraw::DrawProjGroupItem] ProjItem004  label="Rechts"
  CoarseView = false
  Direction = (1,-1e-16,0)
  Focus = 100
  HardHidden = false
  IsoCount = 0
  IsoHidden = false
  IsoVisible = false
  LockPosition = false
  Perspective = false
  Rotation = 0
  RotationVector = (1,0,0)
  ScaleType = 0
  ScrubCount = 1
  SeamHidden = false
  SeamVisible = false
  SmoothHidden = false
  SmoothVisible = true
  Source = -> [Body024]
  Type = 2
  X = -64
  XDirection = (1e-16,1,0)
  Y = 0
FEATURE [TechDraw::DrawProjGroupItem] ProjItem005  label="VorneObenRechts002"
  CoarseView = false
  Direction = (0.57735,-0.57735,0.57735)
  Focus = 100
  HardHidden = false
  IsoCount = 0
  IsoHidden = false
  IsoVisible = false
  LockPosition = false
  Perspective = false
  Rotation = 0
  RotationVector = (1,0,0)
  ScaleType = 0
  ScrubCount = 1
  SeamHidden = false
  SeamVisible = false
  SmoothHidden = false
  SmoothVisible = true
  Source = -> [Body024]
  Type = 7
  X = -1.25771
  XDirection = (0.707107,0.707107,0)
  Y = -90.1346
FEATURE [TechDraw::DrawProjGroup] ProjGroup002
  Anchor = -> View002
  AutoDistribute = false
  LockPosition = false
  ProjectionType = 0
  Rotation = 0
  ScaleType = 0
  Source = -> [Body024]
  Views = -> [View002,ProjItem004,ProjItem005]
  X = 105
  Y = 148.5
  spacingX = 15
  spacingY = 15
FEATURE [TechDraw::DrawViewSection] SectionView  label="Schnitt  - "
  BaseView = -> View002
  CoarseView = false
  CutSurfaceDisplay = 2
  Direction = (1,0,0)
  FileGeomPattern = <path>\data\Mod/TechDraw/PAT/FCPAT.pat
  FileHatchPattern = <path>\data\Mod/TechDraw/Patterns/simple.svg
  Focus = 100
  FuseBeforeCut = false
  HardHidden = false
  HatchOffset = (0,0,0)
  HatchRotation = 0
  HatchScale = 1
  IsoCount = 0
  IsoHidden = false
  IsoVisible = false
  LockPosition = false
  NameGeomPattern = Diamond
  Perspective = false
  Rotation = 90
  ScaleType = 0
  ScrubCount = 1
  SeamHidden = false
  SeamVisible = false
  SectionDirection = 4
  SectionLineStretch = 1
  SectionNormal = (1,0,0)
  SectionOrigin = (0,-96.5,56)
  SmoothHidden = false
  SmoothVisible = true
  Source = -> [Body024]
  TrimAfterCut = false
  UsePreviousCut = false
  X = 169
  XDirection = (0,0,1)
  Y = 148.5
FEATURE [TechDraw::DrawViewAnnotation] Annotation006  label="Beschriftung006"
  Font = osifont
  LineSpace = 100
  LockPosition = false
  MaxWidth = -1
  Rotation = 0
  ScaleType = 0
  Text = Griff Plastik
  TextSize = 5
  TextStyle = 0
  X = 103.742
  Y = 272.18
FEATURE [TechDraw::DrawViewDimension] Dimension009  label="Maß009"
  AngleOverride = false
  Arbitrary = false
  ArbitraryTolerances = false
  BoxCorners = (2) [(-11.5,-24,0),(11.5,24,0)]
  EqualTolerance = true
  ExtensionAngle = 0
  FormatSpec = %.2w
  FormatSpecOverTolerance = %+.2w
  FormatSpecUnderTolerance = %+.2w
  Inverted = false
  LineAngle = 0
  LockPosition = false
  MeasureType = 1
  OverTolerance = 0
  References2D = -> [View002]
  Rotation = 0
  ScaleType = 0
  TheoreticalExact = false
  Type = 1
  UnderTolerance = 0
  X = 0
  Y = 50.4095
FEATURE [TechDraw::DrawViewDimension] Dimension010  label="Maß010"
  AngleOverride = false
  Arbitrary = false
  ArbitraryTolerances = false
  BoxCorners = (2) [(-11.5,-24,0),(11.5,24,0)]
  EqualTolerance = true
  ExtensionAngle = 0
  FormatSpec = %.2w
  FormatSpecOverTolerance = %+.2w
  FormatSpecUnderTolerance = %+.2w
  Inverted = false
  LineAngle = 0
  LockPosition = false
  MeasureType = 1
  OverTolerance = 0
  References2D = -> [View002]
  Rotation = 0
  ScaleType = 0
  TheoreticalExact = false
  Type = 2
  UnderTolerance = 0
  X = 22.027
  Y = 0
FEATURE [TechDraw::DrawViewDimension] Dimension011  label="Maß011"
  AngleOverride = false
  Arbitrary = false
  ArbitraryTolerances = false
  BoxCorners = (2) [(-16.5,-24,0),(16.5,24,0)]
  EqualTolerance = true
  ExtensionAngle = 0
  FormatSpec = %.2w
  FormatSpecOverTolerance = %+.2w
  FormatSpecUnderTolerance = %+.2w
  Inverted = false
  LineAngle = 0
  LockPosition = false
  MeasureType = 1
  OverTolerance = 0
  References2D = -> [ProjItem004]
  Rotation = 0
  ScaleType = 0
  TheoreticalExact = false
  Type = 1
  UnderTolerance = 0
  X = 0
  Y = 50.0289
FEATURE [TechDraw::DrawViewDimension] Dimension012  label="Maß012"
  AngleOverride = false
  Arbitrary = false
  ArbitraryTolerances = false
  BoxCorners = (2) [(-11.5,-24,0),(11.5,24,0)]
  EqualTolerance = true
  ExtensionAngle = 0
  FormatSpec = %.2w
  FormatSpecOverTolerance = %+.2w
  FormatSpecUnderTolerance = %+.2w
  Inverted = false
  LineAngle = 0
  LockPosition = false
  MeasureType = 1
  OverTolerance = 0
  References2D = -> [View002]
  Rotation = 0
  ScaleType = 0
  TheoreticalExact = false
  Type = 0
  UnderTolerance = 0
  X = -24.1227
  Y = 21
FEATURE [TechDraw::DrawViewDimension] Dimension013  label="Maß013"
  AngleOverride = false
  Arbitrary = false
  ArbitraryTolerances = false
  BoxCorners = (2) [(-11.5,-24,0),(11.5,24,0)]
  EqualTolerance = true
  ExtensionAngle = 0
  FormatSpec = %.2w
  FormatSpecOverTolerance = %+.2w
  FormatSpecUnderTolerance = %+.2w
  Inverted = false
  LineAngle = 0
  LockPosition = false
  MeasureType = 1
  OverTolerance = 0
  References2D = -> [View002]
  Rotation = 0
  ScaleType = 0
  TheoreticalExact = false
  Type = 2
  UnderTolerance = 0
  X = -24.1227
  Y = 9.5
FEATURE [TechDraw::DrawViewAnnotation] Annotation007  label="Beschriftung007"
  Font = osifont
  LineSpace = 100
  LockPosition = false
  MaxWidth = -1
  Rotation = 0
  ScaleType = 0
  Text = Bohrungen mittig | tief ansenken
  TextSize = 5
  TextStyle = 0
  X = 103.742
  Y = 219.5
FEATURE [TechDraw::DrawViewAnnotation] Annotation008  label="Beschriftung008"
  Font = osifont
  LineSpace = 100
  LockPosition = false
  MaxWidth = -1
  Rotation = 0
  ScaleType = 0
  Text = Ecke leicht | abrunden
  TextSize = 5
  TextStyle = 0
  X = 37.9187
  Y = 84.9607
FEATURE [TechDraw::DrawViewDimension] Dimension014  label="Maß014"
  AngleOverride = false
  Arbitrary = false
  ArbitraryTolerances = false
  BoxCorners = (2) [(-16.5,-24,0),(16.5,24,0)]
  EqualTolerance = true
  ExtensionAngle = 0
  FormatSpec = %.2w
  FormatSpecOverTolerance = %+.2w
  FormatSpecUnderTolerance = %+.2w
  Inverted = false
  LineAngle = 0
  LockPosition = false
  MeasureType = 1
  OverTolerance = 0
  References2D = -> [ProjItem004]
  Rotation = 0
  ScaleType = 0
  TheoreticalExact = false
  Type = 1
  UnderTolerance = 0
  X = 6.5
  Y = -43.7184
FEATURE [TechDraw::DrawViewDimension] Dimension015  label="Maß015"
  AngleOverride = false
  Arbitrary = false
  ArbitraryTolerances = false
  BoxCorners = (2) [(-16.5,-24,0),(16.5,24,0)]
  EqualTolerance = true
  ExtensionAngle = 0
  FormatSpec = %.2w
  FormatSpecOverTolerance = %+.2w
  FormatSpecUnderTolerance = %+.2w
  Inverted = false
  LineAngle = 0
  LockPosition = false
  MeasureType = 1
  OverTolerance = 0
  References2D = -> [ProjItem004]
  Rotation = 0
  ScaleType = 0
  TheoreticalExact = false
  Type = 2
  UnderTolerance = 0
  X = 25.9305
  Y = -15
FEATURE [TechDraw::DrawViewAnnotation] Annotation009  label="Beschriftung009"
  Font = osifont
  LineSpace = 100
  LockPosition = false
  MaxWidth = -1
  Rotation = 0
  ScaleType = 0
  Text = Maße können leicht abweichen
  TextSize = 5
  TextStyle = 0
  X = 103.742
  Y = 250.5
FEATURE [TechDraw::DrawSVGTemplate] Template003  label="Vorlage003"
  Height = 297
  Orientation = 0
  Template = C:/Program Files/FreeCAD 1.0/data/Mod/TechDraw/Templates/A4_Portrait_blank.svg
  Width = 210
FEATURE [PartDesign::FeatureBase] Clone010
  BaseFeature = -> Body009
  Placement = pos=(0,-25.118,254.583) rot=(1,0,0;0.305433rad)
  Suppressed = false
FEATURE [PartDesign::Body] Body  label="Dach_(clone_Für_Zeichnung)"
  AllowCompound = false
  Group = -> [Clone010]
  Origin = -> Origin
  Placement = pos=(-228,0,0) rot=(1,0,0;5.97775rad)
  Tip = -> Clone010
FEATURE [TechDraw::DrawProjGroupItem] View003  label="Front003"
  CoarseView = false
  Direction = (0,0,1)
  Focus = 100
  HardHidden = false
  IsoCount = 0
  IsoHidden = false
  IsoVisible = false
  LockPosition = true
  Perspective = false
  Rotation = 0
  RotationVector = (1,0,0)
  Scale = 0.75
  ScaleType = 2
  ScrubCount = 1
  SeamHidden = false
  SeamVisible = false
  SmoothHidden = false
  SmoothVisible = true
  Source = -> [Body]
  Type = 0
  X = 0
  XDirection = (1,0,0)
  Y = 0
FEATURE [TechDraw::DrawProjGroupItem] ProjItem006  label="Links003"
  CoarseView = false
  Direction = (-1,0,1e-16)
  Focus = 100
  HardHidden = false
  IsoCount = 0
  IsoHidden = false
  IsoVisible = false
  LockPosition = false
  Perspective = false
  Rotation = 0
  RotationVector = (1,0,0)
  Scale = 0.75
  ScaleType = 2
  ScrubCount = 1
  SeamHidden = false
  SeamVisible = false
  SmoothHidden = false
  SmoothVisible = true
  Source = -> [Body]
  Type = 1
  X = 84.375
  XDirection = (1e-16,0,1)
  Y = 0
FEATURE [TechDraw::DrawProjGroup] ProjGroup003
  Anchor = -> View003
  AutoDistribute = true
  LockPosition = false
  ProjectionType = 0
  Rotation = 0
  Scale = 0.75
  ScaleType = 2
  Source = -> [Body]
  Views = -> [View003,ProjItem006]
  X = 105
  Y = 148.5
  spacingX = 15
  spacingY = 15
FEATURE [TechDraw::DrawViewDimension] Dimension016  label="Maß016"
  AngleOverride = false
  Arbitrary = false
  ArbitraryTolerances = false
  BoxCorners = (2) [(-67.5,-82.5,0),(67.5,82.5,0)]
  EqualTolerance = true
  ExtensionAngle = 0
  FormatSpec = %.2w
  FormatSpecOverTolerance = %+.2w
  FormatSpecUnderTolerance = %+.2w
  Inverted = false
  LineAngle = 0
  LockPosition = false
  MeasureType = 1
  OverTolerance = 0
  References2D = -> [View003]
  Rotation = 0
  ScaleType = 0
  TheoreticalExact = false
  Type = 1
  UnderTolerance = 0
  X = 0
  Y = 96.1088
FEATURE [TechDraw::DrawViewDimension] Dimension017  label="Maß017"
  AngleOverride = false
  Arbitrary = false
  ArbitraryTolerances = false
  BoxCorners = (2) [(-67.5,-82.5,0),(67.5,82.5,0)]
  EqualTolerance = true
  ExtensionAngle = 0
  FormatSpec = %.2w
  FormatSpecOverTolerance = %+.2w
  FormatSpecUnderTolerance = %+.2w
  Inverted = false
  LineAngle = 0
  LockPosition = false
  MeasureType = 1
  OverTolerance = 0
  References2D = -> [View003]
  Rotation = 0
  ScaleType = 0
  TheoreticalExact = false
  Type = 2
  UnderTolerance = 0
  X = -95.2567
  Y = 0
FEATURE [TechDraw::DrawViewDimension] Dimension018  label="Maß018"
  AngleOverride = false
  Arbitrary = false
  ArbitraryTolerances = false
  BoxCorners = (2) [(-67.5,-82.5,0),(67.5,82.5,0)]
  EqualTolerance = true
  ExtensionAngle = 0
  FormatSpec = %.2w
  FormatSpecOverTolerance = %+.2w
  FormatSpecUnderTolerance = %+.2w
  Inverted = false
  LineAngle = 0
  LockPosition = false
  MeasureType = 1
  OverTolerance = 0
  References2D = -> [View003]
  Rotation = 0
  ScaleType = 0
  TheoreticalExact = false
  Type = 0
  UnderTolerance = 0
  X = -78.2396
  Y = -63.75
FEATURE [TechDraw::DrawViewDimension] Dimension019  label="Maß019"
  AngleOverride = false
  Arbitrary = false
  ArbitraryTolerances = false
  BoxCorners = (2) [(-67.5,-82.5,0),(67.5,82.5,0)]
  EqualTolerance = true
  ExtensionAngle = 0
  FormatSpec = %.2w
  FormatSpecOverTolerance = %+.2w
  FormatSpecUnderTolerance = %+.2w
  Inverted = false
  LineAngle = 0
  LockPosition = false
  MeasureType = 1
  OverTolerance = 0
  References2D = -> [View003]
  Rotation = 0
  ScaleType = 0
  TheoreticalExact = false
  Type = 0
  UnderTolerance = 0
  X = -59.625
  Y = -91.8063
FEATURE [TechDraw::DrawViewDimension] Dimension020  label="Maß020"
  AngleOverride = false
  Arbitrary = false
  ArbitraryTolerances = false
  BoxCorners = (2) [(-1.875,-82.5,0),(1.875,82.5,0)]
  EqualTolerance = true
  ExtensionAngle = 0
  FormatSpec = %.2w
  FormatSpecOverTolerance = %+.2w
  FormatSpecUnderTolerance = %+.2w
  Inverted = false
  LineAngle = 0
  LockPosition = false
  MeasureType = 1
  OverTolerance = 0
  References2D = -> [ProjItem006]
  Rotation = 0
  ScaleType = 0
  TheoreticalExact = false
  Type = 1
  UnderTolerance = 0
  X = 0
  Y = 96.2586
FEATURE [TechDraw::DrawViewAnnotation] Annotation010  label="Beschriftung010"
  Font = osifont
  LineSpace = 100
  LockPosition = false
  MaxWidth = -1
  Rotation = 0
  ScaleType = 0
  Text = Dach Plastik
  TextSize = 5
  TextStyle = 0
  X = 105
  Y = 279.5
FEATURE [TechDraw::DrawViewAnnotation] Annotation011  label="Beschriftung011"
  Font = osifont
  LineSpace = 100
  LockPosition = false
  MaxWidth = -1
  Rotation = 0
  ScaleType = 0
  Text = Plattendicke | ca. 5 bis 8 mm
  TextSize = 5
  TextStyle = 0
  X = 184.923
  Y = 261.804
FEATURE [TechDraw::DrawViewAnnotation] Annotation013  label="Beschriftung013"
  Font = osifont
  LineSpace = 100
  LockPosition = false
  MaxWidth = -1
  Rotation = 0
  ScaleType = 0
  Text = 4 Bohrungen symmetrisch angeordnet | ansenken
  TextSize = 5
  TextStyle = 0
  X = 105
  Y = 33.5
FEATURE [TechDraw::DrawSVGTemplate] Template004  label="Vorlage004"
  Height = 297
  Orientation = 0
  Template = C:/Program Files/FreeCAD 1.0/data/Mod/TechDraw/Templates/A4_Portrait_blank.svg
  Width = 210
FEATURE [TechDraw::DrawProjGroupItem] View004  label="Front004"
  CoarseView = false
  Direction = (0,-1,0)
  Focus = 100
  HardHidden = false
  IsoCount = 0
  IsoHidden = false
  IsoVisible = false
  LockPosition = true
  Perspective = false
  Rotation = 0
  RotationVector = (1,0,0)
  Scale = 0.5
  ScaleType = 2
  ScrubCount = 1
  SeamHidden = false
  SeamVisible = false
  SmoothHidden = false
  SmoothVisible = true
  Source = -> [Body025]
  Type = 0
  X = 0
  XDirection = (1,0,0)
  Y = 0
FEATURE [TechDraw::DrawProjGroupItem] ProjItem007  label="Links004"
  CoarseView = false
  Direction = (-1,-1e-16,0)
  Focus = 100
  HardHidden = false
  IsoCount = 0
  IsoHidden = false
  IsoVisible = false
  LockPosition = false
  Perspective = false
  Rotation = 0
  RotationVector = (1,0,0)
  Scale = 0.5
  ScaleType = 2
  ScrubCount = 1
  SeamHidden = false
  SeamVisible = false
  SmoothHidden = false
  SmoothVisible = true
  Source = -> [Body025]
  Type = 1
  X = 57.75
  XDirection = (1e-16,-1,0)
  Y = 0
FEATURE [TechDraw::DrawProjGroup] ProjGroup004
  Anchor = -> View004
  AutoDistribute = false
  LockPosition = false
  ProjectionType = 0
  Rotation = 0
  Scale = 0.5
  ScaleType = 2
  Source = -> [Body025]
  Views = -> [View004,ProjItem007]
  X = 95.5279
  Y = 143.08
  spacingX = 15
  spacingY = 15
FEATURE [TechDraw::DrawViewDimension] Dimension021  label="Maß021"
  AngleOverride = false
  Arbitrary = false
  ArbitraryTolerances = false
  BoxCorners = (2) [(-21.25,-110,0),(21.25,110,0)]
  EqualTolerance = true
  ExtensionAngle = 0
  FormatSpec = %.2w
  FormatSpecOverTolerance = %+.2w
  FormatSpecUnderTolerance = %+.2w
  Inverted = false
  LineAngle = 0
  LockPosition = false
  MeasureType = 1
  OverTolerance = 0
  References2D = -> [View004]
  Rotation = 0
  ScaleType = 0
  TheoreticalExact = false
  Type = 1
  UnderTolerance = 0
  X = 0
  Y = 127.361
FEATURE [TechDraw::DrawViewDimension] Dimension022  label="Maß022"
  AngleOverride = false
  Arbitrary = false
  ArbitraryTolerances = false
  BoxCorners = (2) [(-21.25,-110,0),(21.25,110,0)]
  EqualTolerance = true
  ExtensionAngle = 0
  FormatSpec = %.2w
  FormatSpecOverTolerance = %+.2w
  FormatSpecUnderTolerance = %+.2w
  Inverted = false
  LineAngle = 0
  LockPosition = false
  MeasureType = 1
  OverTolerance = 0
  References2D = -> [View004]
  Rotation = 0
  ScaleType = 0
  TheoreticalExact = false
  Type = 2
  UnderTolerance = 0
  X = -41.8846
  Y = 0
FEATURE [TechDraw::DrawViewDimension] Dimension023  label="Maß023"
  AngleOverride = false
  Arbitrary = false
  ArbitraryTolerances = false
  BoxCorners = (2) [(-2.5,-110,0),(2.5,110,0)]
  EqualTolerance = true
  ExtensionAngle = 0
  FormatSpec = %.2w
  FormatSpecOverTolerance = %+.2w
  FormatSpecUnderTolerance = %+.2w
  Inverted = false
  LineAngle = 0
  LockPosition = false
  MeasureType = 1
  OverTolerance = 0
  References2D = -> [ProjItem007]
  Rotation = 0
  ScaleType = 0
  TheoreticalExact = false
  Type = 1
  UnderTolerance = 0
  X = 0
  Y = 118.353
FEATURE [TechDraw::DrawViewDimension] Dimension024  label="Maß024"
  AngleOverride = false
  Arbitrary = false
  ArbitraryTolerances = false
  BoxCorners = (2) [(-21.25,-110,0),(21.25,110,0)]
  EqualTolerance = true
  ExtensionAngle = 0
  FormatSpec = %.2w
  FormatSpecOverTolerance = %+.2w
  FormatSpecUnderTolerance = %+.2w
  Inverted = false
  LineAngle = 0
  LockPosition = false
  MeasureType = 1
  OverTolerance = 0
  References2D = -> [View004]
  Rotation = 0
  ScaleType = 0
  TheoreticalExact = false
  Type = 0
  UnderTolerance = 0
  X = -16.25
  Y = 116.241
FEATURE [TechDraw::DrawViewDimension] Dimension025  label="Maß025"
  AngleOverride = false
  Arbitrary = false
  ArbitraryTolerances = false
  BoxCorners = (2) [(-21.25,-110,0),(21.25,110,0)]
  EqualTolerance = true
  ExtensionAngle = 0
  FormatSpec = %.2w
  FormatSpecOverTolerance = %+.2w
  FormatSpecUnderTolerance = %+.2w
  Inverted = false
  LineAngle = 0
  LockPosition = false
  MeasureType = 1
  OverTolerance = 0
  References2D = -> [View004]
  Rotation = 0
  ScaleType = 0
  TheoreticalExact = false
  Type = 0
  UnderTolerance = 0
  X = -29.772
  Y = 82.5
FEATURE [TechDraw::DrawViewDimension] Dimension026  label="Maß026"
  AngleOverride = false
  Arbitrary = false
  ArbitraryTolerances = false
  BoxCorners = (2) [(-21.25,-110,0),(21.25,110,0)]
  EqualTolerance = true
  ExtensionAngle = 0
  FormatSpec = %.2w
  FormatSpecOverTolerance = %+.2w
  FormatSpecUnderTolerance = %+.2w
  Inverted = false
  LineAngle = 0
  LockPosition = false
  MeasureType = 1
  OverTolerance = 0
  References2D = -> [View004]
  Rotation = 0
  ScaleType = 0
  TheoreticalExact = false
  Type = 0
  UnderTolerance = 0
  X = 30.4697
  Y = -104.25
FEATURE [TechDraw::DrawViewAnnotation] Annotation014  label="Beschriftung014"
  Font = osifont
  LineSpace = 100
  LockPosition = false
  MaxWidth = -1
  Rotation = 0
  ScaleType = 0
  Text = Brett Rückseite Plastik
  TextSize = 5
  TextStyle = 0
  X = 105
  Y = 286.08
FEATURE [TechDraw::DrawViewAnnotation] Annotation015  label="Beschriftung015"
  Font = osifont
  LineSpace = 100
  LockPosition = false
  MaxWidth = -1
  Rotation = 0
  ScaleType = 0
  Text = Plattendicke | ca. 9 bis 10 mm
  TextSize = 5
  TextStyle = 0
  X = 181.942
  Y = 275.966
FEATURE [TechDraw::DrawViewAnnotation] Annotation016  label="Beschriftung016"
  Font = osifont
  LineSpace = 100
  LockPosition = false
  MaxWidth = -1
  Rotation = 0
  ScaleType = 0
  Text = 4 Bohrungen | Ø 4 mm | symmetrisch | angeordnet | ansenken
  TextSize = 5
  TextStyle = 0
  X = 37.8032
  Y = 177.168
FEATURE [TechDraw::DrawViewAnnotation] Annotation017  label="Beschriftung017"
  Font = osifont
  LineSpace = 100
  LockPosition = false
  MaxWidth = -1
  Rotation = 0
  ScaleType = 0
  Text = 2 Bohrungen Ø 4,5 symmetrisch angeordnet | (für die Alunägel / Baumbefestigung)
  TextSize = 5
  TextStyle = 0
  X = 95.5279
  Y = 14.5167
FEATURE [TechDraw::DrawViewDimension] Dimension027  label="Maß027"
  AngleOverride = false
  Arbitrary = false
  ArbitraryTolerances = false
  BoxCorners = (2) [(-21.25,-110,0),(21.25,110,0)]
  EqualTolerance = true
  ExtensionAngle = 0
  FormatSpec = ⌀%.2w
  FormatSpecOverTolerance = %+.2w
  FormatSpecUnderTolerance = %+.2w
  Inverted = false
  LineAngle = 0
  LockPosition = false
  MeasureType = 1
  OverTolerance = 0
  References2D = -> [View004]
  Rotation = 0
  ScaleType = 0
  TheoreticalExact = false
  Type = 5
  UnderTolerance = 0
  X = -25.5139
  Y = 47.0549
FEATURE [TechDraw::DrawViewDimension] Dimension028  label="Maß028"
  AngleOverride = false
  Arbitrary = false
  ArbitraryTolerances = false
  BoxCorners = (2) [(-21.25,-110,0),(21.25,110,0)]
  EqualTolerance = true
  ExtensionAngle = 0
  FormatSpec = ⌀%.2w
  FormatSpecOverTolerance = %+.2w
  FormatSpecUnderTolerance = %+.2w
  Inverted = false
  LineAngle = 0
  LockPosition = false
  MeasureType = 1
  OverTolerance = 0
  References2D = -> [View004]
  Rotation = 0
  ScaleType = 0
  TheoreticalExact = false
  Type = 5
  UnderTolerance = 0
  X = 28.2287
  Y = 45.1321
FEATURE [TechDraw::DrawViewDimension] Dimension029  label="Maß029"
  AngleOverride = false
  Arbitrary = false
  ArbitraryTolerances = false
  BoxCorners = (2) [(-21.25,-110,0),(21.25,110,0)]
  EqualTolerance = true
  ExtensionAngle = 0
  FormatSpec = ⌀%.2w
  FormatSpecOverTolerance = %+.2w
  FormatSpecUnderTolerance = %+.2w
  Inverted = false
  LineAngle = 0
  LockPosition = false
  MeasureType = 1
  OverTolerance = 0
  References2D = -> [View004]
  Rotation = 0
  ScaleType = 0
  TheoreticalExact = false
  Type = 5
  UnderTolerance = 0
  X = -29.347
  Y = -64.2374
FEATURE [TechDraw::DrawViewDimension] Dimension030  label="Maß030"
  AngleOverride = false
  Arbitrary = false
  ArbitraryTolerances = false
  BoxCorners = (2) [(-21.25,-110,0),(21.25,110,0)]
  EqualTolerance = true
  ExtensionAngle = 0
  FormatSpec = ⌀%.2w
  FormatSpecOverTolerance = %+.2w
  FormatSpecUnderTolerance = %+.2w
  Inverted = false
  LineAngle = 0
  LockPosition = false
  MeasureType = 1
  OverTolerance = 0
  References2D = -> [View004]
  Rotation = 0
  ScaleType = 0
  TheoreticalExact = false
  Type = 5
  UnderTolerance = 0
  X = 31.1799
  Y = -68.1494
FEATURE [TechDraw::DrawViewDimension] Dimension031  label="Maß031"
  AngleOverride = false
  Arbitrary = false
  ArbitraryTolerances = false
  BoxCorners = (2) [(-21.25,-110,0),(21.25,110,0)]
  EqualTolerance = true
  ExtensionAngle = 0
  FormatSpec = ⌀%.2w
  FormatSpecOverTolerance = %+.2w
  FormatSpecUnderTolerance = %+.2w
  Inverted = false
  LineAngle = 0
  LockPosition = false
  MeasureType = 1
  OverTolerance = 0
  References2D = -> [View004]
  Rotation = 0
  ScaleType = 0
  TheoreticalExact = false
  Type = 5
  UnderTolerance = 0
  X = -30.387
  Y = -101.172
FEATURE [TechDraw::DrawViewDimension] Dimension032  label="Maß032"
  AngleOverride = false
  Arbitrary = false
  ArbitraryTolerances = false
  BoxCorners = (2) [(-21.25,-110,0),(21.25,110,0)]
  EqualTolerance = true
  ExtensionAngle = 0
  FormatSpec = ⌀%.2w
  FormatSpecOverTolerance = %+.2w
  FormatSpecUnderTolerance = %+.2w
  Inverted = false
  LineAngle = 0
  LockPosition = false
  MeasureType = 1
  OverTolerance = 0
  References2D = -> [View004]
  Rotation = 0
  ScaleType = 0
  TheoreticalExact = false
  Type = 5
  UnderTolerance = 0
  X = 31.8396
  Y = 94.6436
FEATURE [TechDraw::DrawPage] Page004  label="Brett_Rückseite_Zeichnung"
  KeepUpdated = true
  NextBalloonIndex = 1
  ProjectionType = 0
  Template = -> Template004
  Views = -> [ProjGroup004,Dimension021,Dimension022,Dimension023,Dimension024,Dimension025,Dimension026,Annotation014,Annotation015,Annotation016,Annotation017,Dimension027,Dimension028,Dimension029,Dimension030,Dimension031,Dimension032]
FEATURE [TechDraw::DrawViewDimension] Dimension033  label="Maß033"
  AngleOverride = false
  Arbitrary = false
  ArbitraryTolerances = false
  BoxCorners = (2) [(-78,-22.5,0),(78,22.5,0)]
  EqualTolerance = true
  ExtensionAngle = 0
  FormatSpec = ⌀%.2w
  FormatSpecOverTolerance = %+.2w
  FormatSpecUnderTolerance = %+.2w
  Inverted = false
  LineAngle = 0
  LockPosition = false
  MeasureType = 1
  OverTolerance = 0
  References2D = -> [View]
  Rotation = 0
  ScaleType = 0
  TheoreticalExact = false
  Type = 5
  UnderTolerance = 0
  X = -41.8564
  Y = -30.7704
FEATURE [TechDraw::DrawPage] Page  label="Frontplatte_Plastik_Zeichnung"
  KeepUpdated = true
  NextBalloonIndex = 1
  ProjectionType = 0
  Template = -> Template
  Views = -> [ProjGroup,Dimension,Dimension001,Dimension002,Dimension003,Dimension004,Annotation,Annotation001,Annotation005,Dimension033]
FEATURE [TechDraw::DrawViewDimension] Dimension034  label="Maß034"
  AngleOverride = false
  Arbitrary = false
  ArbitraryTolerances = false
  BoxCorners = (2) [(-9,-22.5,0),(9,22.5,0)]
  EqualTolerance = true
  ExtensionAngle = 0
  FormatSpec = ⌀%.2w
  FormatSpecOverTolerance = %+.2w
  FormatSpecUnderTolerance = %+.2w
  Inverted = false
  LineAngle = 0
  LockPosition = false
  MeasureType = 1
  OverTolerance = 0
  References2D = -> [View001]
  Rotation = 0
  ScaleType = 0
  TheoreticalExact = false
  Type = 5
  UnderTolerance = 0
  X = -23.1671
  Y = 6.69801
FEATURE [TechDraw::DrawPage] Page001  label="Drehbarer_Halter_Zeichnung"
  KeepUpdated = true
  NextBalloonIndex = 1
  ProjectionType = 0
  Template = -> Template001
  Views = -> [ProjGroup001,Dimension005,Dimension006,Dimension007,Dimension008,Annotation002,Annotation003,Annotation004,Dimension034]
FEATURE [TechDraw::DrawViewDimension] Dimension035  label="Maß035"
  AngleOverride = false
  Arbitrary = false
  ArbitraryTolerances = false
  BoxCorners = (2) [(-11.5,-24,0),(11.5,24,0)]
  EqualTolerance = true
  ExtensionAngle = 0
  FormatSpec = ⌀%.2w
  FormatSpecOverTolerance = %+.2w
  FormatSpecUnderTolerance = %+.2w
  Inverted = false
  LineAngle = 0
  LockPosition = false
  MeasureType = 1
  OverTolerance = 0
  References2D = -> [View002]
  Rotation = 0
  ScaleType = 0
  TheoreticalExact = false
  Type = 5
  UnderTolerance = 0
  X = 30.4427
  Y = 45.4445
FEATURE [TechDraw::DrawPage] Page002  label="Griff_Zeichnung"
  KeepUpdated = true
  NextBalloonIndex = 1
  ProjectionType = 0
  Template = -> Template002
  Views = -> [ProjGroup002,SectionView,Annotation006,Dimension009,Dimension010,Dimension011,Dimension012,Dimension013,Annotation007,Annotation008,Dimension014,Dimension015,Annotation009,Dimension035]
FEATURE [TechDraw::DrawViewDimension] Dimension036  label="Maß036"
  AngleOverride = false
  Arbitrary = false
  ArbitraryTolerances = false
  BoxCorners = (2) [(-67.5,-82.5,0),(67.5,82.5,0)]
  EqualTolerance = true
  ExtensionAngle = 0
  FormatSpec = ⌀%.2w
  FormatSpecOverTolerance = %+.2w
  FormatSpecUnderTolerance = %+.2w
  Inverted = false
  LineAngle = 0
  LockPosition = false
  MeasureType = 1
  OverTolerance = 0
  References2D = -> [View003]
  Rotation = 0
  ScaleType = 0
  TheoreticalExact = false
  Type = 5
  UnderTolerance = 0
  X = -76.299
  Y = -27.4518
FEATURE [TechDraw::DrawPage] Page003  label="Dach_Zeichnung"
  KeepUpdated = true
  NextBalloonIndex = 1
  ProjectionType = 0
  Template = -> Template003
  Views = -> [ProjGroup003,Dimension016,Dimension017,Dimension018,Dimension019,Dimension020,Annotation010,Annotation011,Annotation013,Dimension036]
FEATURE [App::DocumentObjectGroup] Group006  label="Zeichnungen"
  Group = -> [Page,Page001,Page002,Page003,Body,Page004]
note: 2 file-system paths scrubbed to <path> (originals preserved in the JSON sidecar)
